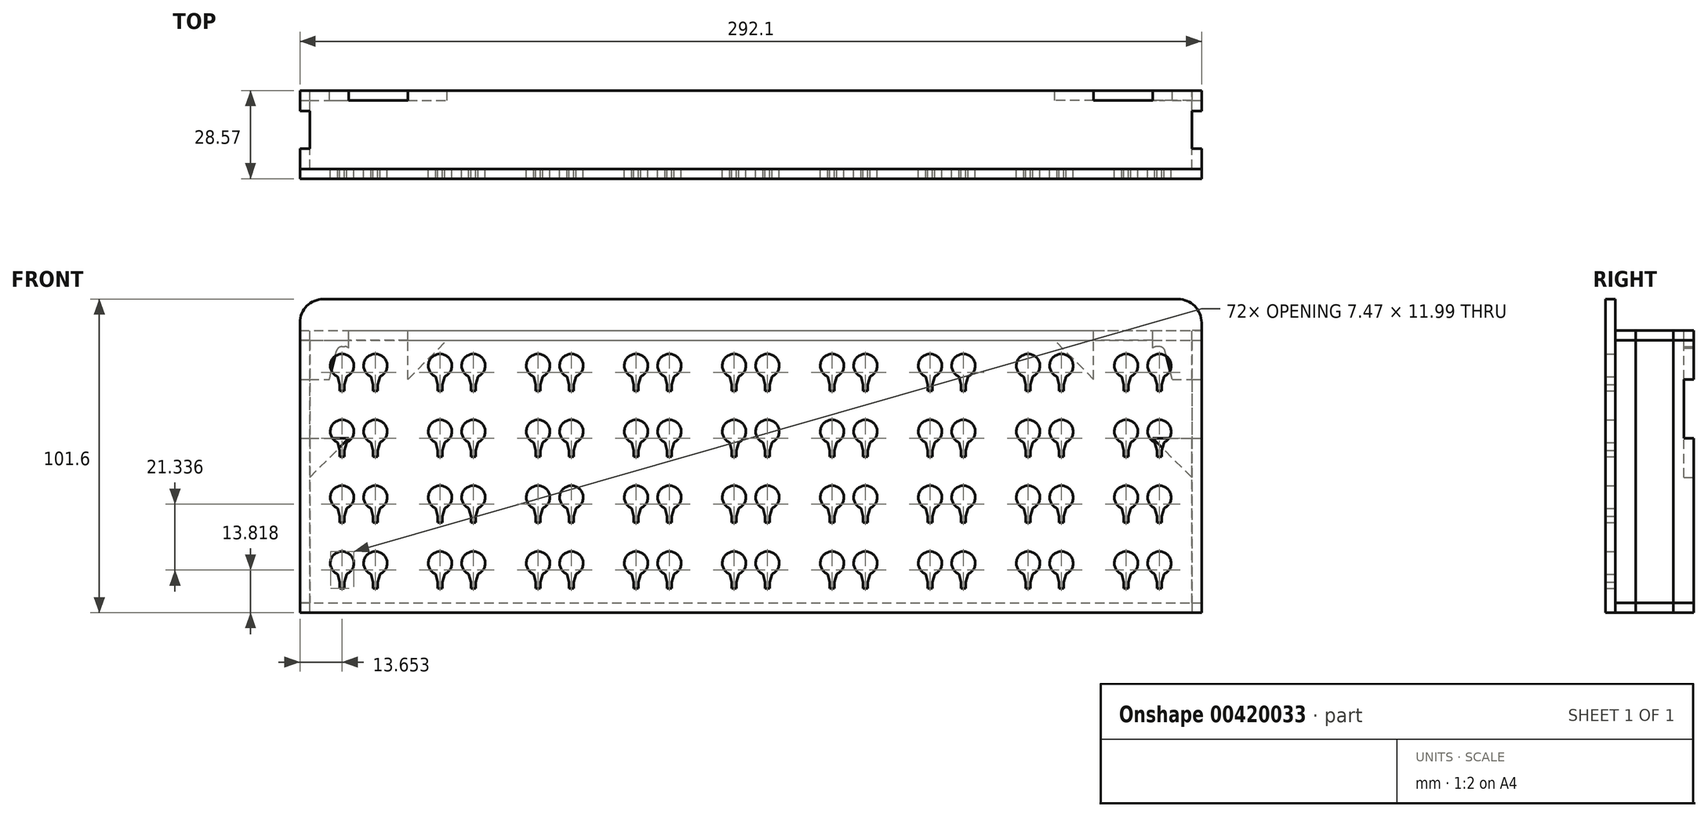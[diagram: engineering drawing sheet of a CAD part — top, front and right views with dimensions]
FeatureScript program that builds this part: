
annotation { "Feature Type Name" : "Feature", "Feature Type Description" : "" }
export const myFeature = defineFeature(function(context is Context, id is Id, definition is map)
    precondition{}
    {
        {
            var Q0;
            Q0=qCreatedBy(makeId("Front.planeOp"),FACE);
            var sketch = newSketch(context, id + "F0", { "sketchPlane" : qUnion([Q0])});
            skLineSegment(sketch, "E0.bottom", {"start": v(146.05, 50.8) * mm, "end": v(-146.05, 50.8) * mm});
            skLineSegment(sketch, "E0.top", {"start": v(146.05, -50.8) * mm, "end": v(-146.05, -50.8) * mm});
            skLineSegment(sketch, "E0.left", {"start": v(146.05, 50.8) * mm, "end": v(146.05, -50.8) * mm});
            skLineSegment(sketch, "E0.right", {"start": v(-146.05, 50.8) * mm, "end": v(-146.05, -50.8) * mm});
            skPoint(sketch, "E0.middle", {"position": v(0, 0) * mm});
            skLineSegment(sketch, "E1", {"start": v(-146.05, 29.21) * mm, "end": v(146.05, 29.21) * mm, "construction": true});
            skArc(sketch, "E2", {"start": v(-4.64, 25.48) * mm, "mid": v(-5.4, 33.02) * mm, "end": v(-6.16, 25.48) * mm});
            skLineSegment(sketch, "E3.bottom", {"start": v(-4.64, 21.03) * mm, "end": v(-6.16, 21.03) * mm});
            skLineSegment(sketch, "E3.left", {"start": v(-4.64, 21.03) * mm, "end": v(-4.64, 25.48) * mm});
            skLineSegment(sketch, "E3.right", {"start": v(-6.16, 21.03) * mm, "end": v(-6.16, 25.48) * mm});
            skPoint(sketch, "E3.middle", {"position": v(-5.4, 25.4) * mm});
            skLineSegment(sketch, "E4", {"start": v(0, 50.8) * mm, "end": v(0, -50.8) * mm, "construction": true});
            skLineSegment(sketch, "E5.MirrorCS", {"start": v(4.64, 21.03) * mm, "end": v(6.16, 21.03) * mm});
            skLineSegment(sketch, "E6.MirrorCS", {"start": v(4.64, 21.03) * mm, "end": v(4.64, 25.48) * mm});
            skLineSegment(sketch, "E7.MirrorCS", {"start": v(6.16, 21.03) * mm, "end": v(6.16, 25.48) * mm});
            skArc(sketch, "E8.MirrorCS", {"start": v(4.64, 25.48) * mm, "mid": v(5.4, 33.02) * mm, "end": v(6.16, 25.48) * mm});
            skArc(sketch, "E9.0.1.0", {"start": v(-4.64, 4.14) * mm, "mid": v(-5.4, 11.68) * mm, "end": v(-6.16, 4.14) * mm});
            skLineSegment(sketch, "E9.0.1.1", {"start": v(-4.64, -0.3) * mm, "end": v(-4.64, 4.14) * mm});
            skLineSegment(sketch, "E9.0.1.2", {"start": v(-4.64, -0.3) * mm, "end": v(-6.16, -0.3) * mm});
            skLineSegment(sketch, "E9.0.1.3", {"start": v(-6.16, -0.3) * mm, "end": v(-6.16, 4.14) * mm});
            skArc(sketch, "E9.0.1.4", {"start": v(4.64, 4.14) * mm, "mid": v(5.4, 11.68) * mm, "end": v(6.16, 4.14) * mm});
            skLineSegment(sketch, "E9.0.1.5", {"start": v(4.64, -0.3) * mm, "end": v(4.64, 4.14) * mm});
            skLineSegment(sketch, "E9.0.1.6", {"start": v(4.64, -0.3) * mm, "end": v(6.16, -0.3) * mm});
            skLineSegment(sketch, "E9.0.1.7", {"start": v(6.16, -0.3) * mm, "end": v(6.16, 4.14) * mm});
            skArc(sketch, "E9.0.2.0", {"start": v(-4.64, -17.2) * mm, "mid": v(-5.4, -9.65) * mm, "end": v(-6.16, -17.2) * mm});
            skLineSegment(sketch, "E9.0.2.1", {"start": v(-4.64, -21.64) * mm, "end": v(-4.64, -17.2) * mm});
            skLineSegment(sketch, "E9.0.2.2", {"start": v(-4.64, -21.64) * mm, "end": v(-6.16, -21.64) * mm});
            skLineSegment(sketch, "E9.0.2.3", {"start": v(-6.16, -21.64) * mm, "end": v(-6.16, -17.2) * mm});
            skArc(sketch, "E9.0.2.4", {"start": v(4.64, -17.2) * mm, "mid": v(5.4, -9.65) * mm, "end": v(6.16, -17.2) * mm});
            skLineSegment(sketch, "E9.0.2.5", {"start": v(4.64, -21.64) * mm, "end": v(4.64, -17.2) * mm});
            skLineSegment(sketch, "E9.0.2.6", {"start": v(4.64, -21.64) * mm, "end": v(6.16, -21.64) * mm});
            skLineSegment(sketch, "E9.0.2.7", {"start": v(6.16, -21.64) * mm, "end": v(6.16, -17.2) * mm});
            skArc(sketch, "E9.0.3.0", {"start": v(-4.64, -38.53) * mm, "mid": v(-5.4, -30.99) * mm, "end": v(-6.16, -38.53) * mm});
            skLineSegment(sketch, "E9.0.3.1", {"start": v(-4.64, -42.98) * mm, "end": v(-4.64, -38.53) * mm});
            skLineSegment(sketch, "E9.0.3.2", {"start": v(-4.64, -42.98) * mm, "end": v(-6.16, -42.98) * mm});
            skLineSegment(sketch, "E9.0.3.3", {"start": v(-6.16, -42.98) * mm, "end": v(-6.16, -38.53) * mm});
            skArc(sketch, "E9.0.3.4", {"start": v(4.64, -38.53) * mm, "mid": v(5.4, -30.99) * mm, "end": v(6.16, -38.53) * mm});
            skLineSegment(sketch, "E9.0.3.5", {"start": v(4.64, -42.98) * mm, "end": v(4.64, -38.53) * mm});
            skLineSegment(sketch, "E9.0.3.6", {"start": v(4.64, -42.98) * mm, "end": v(6.16, -42.98) * mm});
            skLineSegment(sketch, "E9.0.3.7", {"start": v(6.16, -42.98) * mm, "end": v(6.16, -38.53) * mm});
            skArc(sketch, "E9.1.0.0", {"start": v(27.11, 25.48) * mm, "mid": v(26.35, 33.02) * mm, "end": v(25.6, 25.48) * mm});
            skLineSegment(sketch, "E9.1.0.1", {"start": v(27.11, 21.03) * mm, "end": v(27.11, 25.48) * mm});
            skLineSegment(sketch, "E9.1.0.2", {"start": v(27.11, 21.03) * mm, "end": v(25.6, 21.03) * mm});
            skLineSegment(sketch, "E9.1.0.3", {"start": v(25.6, 21.03) * mm, "end": v(25.6, 25.48) * mm});
            skArc(sketch, "E9.1.0.4", {"start": v(36.39, 25.48) * mm, "mid": v(37.15, 33.02) * mm, "end": v(37.9, 25.48) * mm});
            skLineSegment(sketch, "E9.1.0.5", {"start": v(36.39, 21.03) * mm, "end": v(36.39, 25.48) * mm});
            skLineSegment(sketch, "E9.1.0.6", {"start": v(36.39, 21.03) * mm, "end": v(37.9, 21.03) * mm});
            skLineSegment(sketch, "E9.1.0.7", {"start": v(37.9, 21.03) * mm, "end": v(37.9, 25.48) * mm});
            skArc(sketch, "E9.1.1.0", {"start": v(27.11, 4.14) * mm, "mid": v(26.35, 11.68) * mm, "end": v(25.6, 4.14) * mm});
            skLineSegment(sketch, "E9.1.1.1", {"start": v(27.11, -0.3) * mm, "end": v(27.11, 4.14) * mm});
            skLineSegment(sketch, "E9.1.1.2", {"start": v(27.11, -0.3) * mm, "end": v(25.6, -0.3) * mm});
            skLineSegment(sketch, "E9.1.1.3", {"start": v(25.6, -0.3) * mm, "end": v(25.6, 4.14) * mm});
            skArc(sketch, "E9.1.1.4", {"start": v(36.39, 4.14) * mm, "mid": v(37.15, 11.68) * mm, "end": v(37.9, 4.14) * mm});
            skLineSegment(sketch, "E9.1.1.5", {"start": v(36.39, -0.3) * mm, "end": v(36.39, 4.14) * mm});
            skLineSegment(sketch, "E9.1.1.6", {"start": v(36.39, -0.3) * mm, "end": v(37.9, -0.3) * mm});
            skLineSegment(sketch, "E9.1.1.7", {"start": v(37.9, -0.3) * mm, "end": v(37.9, 4.14) * mm});
            skArc(sketch, "E9.1.2.0", {"start": v(27.11, -17.2) * mm, "mid": v(26.35, -9.65) * mm, "end": v(25.6, -17.2) * mm});
            skLineSegment(sketch, "E9.1.2.1", {"start": v(27.11, -21.64) * mm, "end": v(27.11, -17.2) * mm});
            skLineSegment(sketch, "E9.1.2.2", {"start": v(27.11, -21.64) * mm, "end": v(25.6, -21.64) * mm});
            skLineSegment(sketch, "E9.1.2.3", {"start": v(25.6, -21.64) * mm, "end": v(25.6, -17.2) * mm});
            skArc(sketch, "E9.1.2.4", {"start": v(36.39, -17.2) * mm, "mid": v(37.15, -9.65) * mm, "end": v(37.9, -17.2) * mm});
            skLineSegment(sketch, "E9.1.2.5", {"start": v(36.39, -21.64) * mm, "end": v(36.39, -17.2) * mm});
            skLineSegment(sketch, "E9.1.2.6", {"start": v(36.39, -21.64) * mm, "end": v(37.9, -21.64) * mm});
            skLineSegment(sketch, "E9.1.2.7", {"start": v(37.9, -21.64) * mm, "end": v(37.9, -17.2) * mm});
            skArc(sketch, "E9.1.3.0", {"start": v(27.11, -38.53) * mm, "mid": v(26.35, -30.99) * mm, "end": v(25.6, -38.53) * mm});
            skLineSegment(sketch, "E9.1.3.1", {"start": v(27.11, -42.98) * mm, "end": v(27.11, -38.53) * mm});
            skLineSegment(sketch, "E9.1.3.2", {"start": v(27.11, -42.98) * mm, "end": v(25.6, -42.98) * mm});
            skLineSegment(sketch, "E9.1.3.3", {"start": v(25.6, -42.98) * mm, "end": v(25.6, -38.53) * mm});
            skArc(sketch, "E9.1.3.4", {"start": v(36.39, -38.53) * mm, "mid": v(37.15, -30.99) * mm, "end": v(37.9, -38.53) * mm});
            skLineSegment(sketch, "E9.1.3.5", {"start": v(36.39, -42.98) * mm, "end": v(36.39, -38.53) * mm});
            skLineSegment(sketch, "E9.1.3.6", {"start": v(36.39, -42.98) * mm, "end": v(37.9, -42.98) * mm});
            skLineSegment(sketch, "E9.1.3.7", {"start": v(37.9, -42.98) * mm, "end": v(37.9, -38.53) * mm});
            skArc(sketch, "E9.2.0.0", {"start": v(58.86, 25.48) * mm, "mid": v(58.1, 33.02) * mm, "end": v(57.34, 25.48) * mm});
            skLineSegment(sketch, "E9.2.0.1", {"start": v(58.86, 21.03) * mm, "end": v(58.86, 25.48) * mm});
            skLineSegment(sketch, "E9.2.0.2", {"start": v(58.86, 21.03) * mm, "end": v(57.34, 21.03) * mm});
            skLineSegment(sketch, "E9.2.0.3", {"start": v(57.34, 21.03) * mm, "end": v(57.34, 25.48) * mm});
            skArc(sketch, "E9.2.0.4", {"start": v(68.14, 25.48) * mm, "mid": v(68.9, 33.02) * mm, "end": v(69.66, 25.48) * mm});
            skLineSegment(sketch, "E9.2.0.5", {"start": v(68.14, 21.03) * mm, "end": v(68.14, 25.48) * mm});
            skLineSegment(sketch, "E9.2.0.6", {"start": v(68.14, 21.03) * mm, "end": v(69.66, 21.03) * mm});
            skLineSegment(sketch, "E9.2.0.7", {"start": v(69.66, 21.03) * mm, "end": v(69.66, 25.48) * mm});
            skArc(sketch, "E9.2.1.0", {"start": v(58.86, 4.14) * mm, "mid": v(58.1, 11.68) * mm, "end": v(57.34, 4.14) * mm});
            skLineSegment(sketch, "E9.2.1.1", {"start": v(58.86, -0.3) * mm, "end": v(58.86, 4.14) * mm});
            skLineSegment(sketch, "E9.2.1.2", {"start": v(58.86, -0.3) * mm, "end": v(57.34, -0.3) * mm});
            skLineSegment(sketch, "E9.2.1.3", {"start": v(57.34, -0.3) * mm, "end": v(57.34, 4.14) * mm});
            skArc(sketch, "E9.2.1.4", {"start": v(68.14, 4.14) * mm, "mid": v(68.9, 11.68) * mm, "end": v(69.66, 4.14) * mm});
            skLineSegment(sketch, "E9.2.1.5", {"start": v(68.14, -0.3) * mm, "end": v(68.14, 4.14) * mm});
            skLineSegment(sketch, "E9.2.1.6", {"start": v(68.14, -0.3) * mm, "end": v(69.66, -0.3) * mm});
            skLineSegment(sketch, "E9.2.1.7", {"start": v(69.66, -0.3) * mm, "end": v(69.66, 4.14) * mm});
            skArc(sketch, "E9.2.2.0", {"start": v(58.86, -17.2) * mm, "mid": v(58.1, -9.65) * mm, "end": v(57.34, -17.2) * mm});
            skLineSegment(sketch, "E9.2.2.1", {"start": v(58.86, -21.64) * mm, "end": v(58.86, -17.2) * mm});
            skLineSegment(sketch, "E9.2.2.2", {"start": v(58.86, -21.64) * mm, "end": v(57.34, -21.64) * mm});
            skLineSegment(sketch, "E9.2.2.3", {"start": v(57.34, -21.64) * mm, "end": v(57.34, -17.2) * mm});
            skArc(sketch, "E9.2.2.4", {"start": v(68.14, -17.2) * mm, "mid": v(68.9, -9.65) * mm, "end": v(69.66, -17.2) * mm});
            skLineSegment(sketch, "E9.2.2.5", {"start": v(68.14, -21.64) * mm, "end": v(68.14, -17.2) * mm});
            skLineSegment(sketch, "E9.2.2.6", {"start": v(68.14, -21.64) * mm, "end": v(69.66, -21.64) * mm});
            skLineSegment(sketch, "E9.2.2.7", {"start": v(69.66, -21.64) * mm, "end": v(69.66, -17.2) * mm});
            skArc(sketch, "E9.2.3.0", {"start": v(58.86, -38.53) * mm, "mid": v(58.1, -30.99) * mm, "end": v(57.34, -38.53) * mm});
            skLineSegment(sketch, "E9.2.3.1", {"start": v(58.86, -42.98) * mm, "end": v(58.86, -38.53) * mm});
            skLineSegment(sketch, "E9.2.3.2", {"start": v(58.86, -42.98) * mm, "end": v(57.34, -42.98) * mm});
            skLineSegment(sketch, "E9.2.3.3", {"start": v(57.34, -42.98) * mm, "end": v(57.34, -38.53) * mm});
            skArc(sketch, "E9.2.3.4", {"start": v(68.14, -38.53) * mm, "mid": v(68.9, -30.99) * mm, "end": v(69.66, -38.53) * mm});
            skLineSegment(sketch, "E9.2.3.5", {"start": v(68.14, -42.98) * mm, "end": v(68.14, -38.53) * mm});
            skLineSegment(sketch, "E9.2.3.6", {"start": v(68.14, -42.98) * mm, "end": v(69.66, -42.98) * mm});
            skLineSegment(sketch, "E9.2.3.7", {"start": v(69.66, -42.98) * mm, "end": v(69.66, -38.53) * mm});
            skArc(sketch, "E9.3.0.0", {"start": v(90.61, 25.48) * mm, "mid": v(89.85, 33.02) * mm, "end": v(89.1, 25.48) * mm});
            skLineSegment(sketch, "E9.3.0.1", {"start": v(90.61, 21.03) * mm, "end": v(90.61, 25.48) * mm});
            skLineSegment(sketch, "E9.3.0.2", {"start": v(90.61, 21.03) * mm, "end": v(89.1, 21.03) * mm});
            skLineSegment(sketch, "E9.3.0.3", {"start": v(89.1, 21.03) * mm, "end": v(89.1, 25.48) * mm});
            skArc(sketch, "E9.3.0.4", {"start": v(99.89, 25.48) * mm, "mid": v(100.65, 33.02) * mm, "end": v(101.4, 25.48) * mm});
            skLineSegment(sketch, "E9.3.0.5", {"start": v(99.89, 21.03) * mm, "end": v(99.89, 25.48) * mm});
            skLineSegment(sketch, "E9.3.0.6", {"start": v(99.89, 21.03) * mm, "end": v(101.4, 21.03) * mm});
            skLineSegment(sketch, "E9.3.0.7", {"start": v(101.4, 21.03) * mm, "end": v(101.4, 25.48) * mm});
            skArc(sketch, "E9.3.1.0", {"start": v(90.61, 4.14) * mm, "mid": v(89.85, 11.68) * mm, "end": v(89.1, 4.14) * mm});
            skLineSegment(sketch, "E9.3.1.1", {"start": v(90.61, -0.3) * mm, "end": v(90.61, 4.14) * mm});
            skLineSegment(sketch, "E9.3.1.2", {"start": v(90.61, -0.3) * mm, "end": v(89.1, -0.3) * mm});
            skLineSegment(sketch, "E9.3.1.3", {"start": v(89.1, -0.3) * mm, "end": v(89.1, 4.14) * mm});
            skArc(sketch, "E9.3.1.4", {"start": v(99.89, 4.14) * mm, "mid": v(100.65, 11.68) * mm, "end": v(101.4, 4.14) * mm});
            skLineSegment(sketch, "E9.3.1.5", {"start": v(99.89, -0.3) * mm, "end": v(99.89, 4.14) * mm});
            skLineSegment(sketch, "E9.3.1.6", {"start": v(99.89, -0.3) * mm, "end": v(101.4, -0.3) * mm});
            skLineSegment(sketch, "E9.3.1.7", {"start": v(101.4, -0.3) * mm, "end": v(101.4, 4.14) * mm});
            skArc(sketch, "E9.3.2.0", {"start": v(90.61, -17.2) * mm, "mid": v(89.85, -9.65) * mm, "end": v(89.1, -17.2) * mm});
            skLineSegment(sketch, "E9.3.2.1", {"start": v(90.61, -21.64) * mm, "end": v(90.61, -17.2) * mm});
            skLineSegment(sketch, "E9.3.2.2", {"start": v(90.61, -21.64) * mm, "end": v(89.1, -21.64) * mm});
            skLineSegment(sketch, "E9.3.2.3", {"start": v(89.1, -21.64) * mm, "end": v(89.1, -17.2) * mm});
            skArc(sketch, "E9.3.2.4", {"start": v(99.89, -17.2) * mm, "mid": v(100.65, -9.65) * mm, "end": v(101.4, -17.2) * mm});
            skLineSegment(sketch, "E9.3.2.5", {"start": v(99.89, -21.64) * mm, "end": v(99.89, -17.2) * mm});
            skLineSegment(sketch, "E9.3.2.6", {"start": v(99.89, -21.64) * mm, "end": v(101.4, -21.64) * mm});
            skLineSegment(sketch, "E9.3.2.7", {"start": v(101.4, -21.64) * mm, "end": v(101.4, -17.2) * mm});
            skArc(sketch, "E9.3.3.0", {"start": v(90.61, -38.53) * mm, "mid": v(89.85, -30.99) * mm, "end": v(89.1, -38.53) * mm});
            skLineSegment(sketch, "E9.3.3.1", {"start": v(90.61, -42.98) * mm, "end": v(90.61, -38.53) * mm});
            skLineSegment(sketch, "E9.3.3.2", {"start": v(90.61, -42.98) * mm, "end": v(89.1, -42.98) * mm});
            skLineSegment(sketch, "E9.3.3.3", {"start": v(89.1, -42.98) * mm, "end": v(89.1, -38.53) * mm});
            skArc(sketch, "E9.3.3.4", {"start": v(99.89, -38.53) * mm, "mid": v(100.65, -30.99) * mm, "end": v(101.4, -38.53) * mm});
            skLineSegment(sketch, "E9.3.3.5", {"start": v(99.89, -42.98) * mm, "end": v(99.89, -38.53) * mm});
            skLineSegment(sketch, "E9.3.3.6", {"start": v(99.89, -42.98) * mm, "end": v(101.4, -42.98) * mm});
            skLineSegment(sketch, "E9.3.3.7", {"start": v(101.4, -42.98) * mm, "end": v(101.4, -38.53) * mm});
            skArc(sketch, "E9.4.0.0", {"start": v(122.36, 25.48) * mm, "mid": v(121.6, 33.02) * mm, "end": v(120.84, 25.48) * mm});
            skLineSegment(sketch, "E9.4.0.1", {"start": v(122.36, 21.03) * mm, "end": v(122.36, 25.48) * mm});
            skLineSegment(sketch, "E9.4.0.2", {"start": v(122.36, 21.03) * mm, "end": v(120.84, 21.03) * mm});
            skLineSegment(sketch, "E9.4.0.3", {"start": v(120.84, 21.03) * mm, "end": v(120.84, 25.48) * mm});
            skArc(sketch, "E9.4.0.4", {"start": v(131.64, 25.48) * mm, "mid": v(132.4, 33.02) * mm, "end": v(133.16, 25.48) * mm});
            skLineSegment(sketch, "E9.4.0.5", {"start": v(131.64, 21.03) * mm, "end": v(131.64, 25.48) * mm});
            skLineSegment(sketch, "E9.4.0.6", {"start": v(131.64, 21.03) * mm, "end": v(133.16, 21.03) * mm});
            skLineSegment(sketch, "E9.4.0.7", {"start": v(133.16, 21.03) * mm, "end": v(133.16, 25.48) * mm});
            skArc(sketch, "E9.4.1.0", {"start": v(122.36, 4.14) * mm, "mid": v(121.6, 11.68) * mm, "end": v(120.84, 4.14) * mm});
            skLineSegment(sketch, "E9.4.1.1", {"start": v(122.36, -0.3) * mm, "end": v(122.36, 4.14) * mm});
            skLineSegment(sketch, "E9.4.1.2", {"start": v(122.36, -0.3) * mm, "end": v(120.84, -0.3) * mm});
            skLineSegment(sketch, "E9.4.1.3", {"start": v(120.84, -0.3) * mm, "end": v(120.84, 4.14) * mm});
            skArc(sketch, "E9.4.1.4", {"start": v(131.64, 4.14) * mm, "mid": v(132.4, 11.68) * mm, "end": v(133.16, 4.14) * mm});
            skLineSegment(sketch, "E9.4.1.5", {"start": v(131.64, -0.3) * mm, "end": v(131.64, 4.14) * mm});
            skLineSegment(sketch, "E9.4.1.6", {"start": v(131.64, -0.3) * mm, "end": v(133.16, -0.3) * mm});
            skLineSegment(sketch, "E9.4.1.7", {"start": v(133.16, -0.3) * mm, "end": v(133.16, 4.14) * mm});
            skArc(sketch, "E9.4.2.0", {"start": v(122.36, -17.2) * mm, "mid": v(121.6, -9.65) * mm, "end": v(120.84, -17.2) * mm});
            skLineSegment(sketch, "E9.4.2.1", {"start": v(122.36, -21.64) * mm, "end": v(122.36, -17.2) * mm});
            skLineSegment(sketch, "E9.4.2.2", {"start": v(122.36, -21.64) * mm, "end": v(120.84, -21.64) * mm});
            skLineSegment(sketch, "E9.4.2.3", {"start": v(120.84, -21.64) * mm, "end": v(120.84, -17.2) * mm});
            skArc(sketch, "E9.4.2.4", {"start": v(131.64, -17.2) * mm, "mid": v(132.4, -9.65) * mm, "end": v(133.16, -17.2) * mm});
            skLineSegment(sketch, "E9.4.2.5", {"start": v(131.64, -21.64) * mm, "end": v(131.64, -17.2) * mm});
            skLineSegment(sketch, "E9.4.2.6", {"start": v(131.64, -21.64) * mm, "end": v(133.16, -21.64) * mm});
            skLineSegment(sketch, "E9.4.2.7", {"start": v(133.16, -21.64) * mm, "end": v(133.16, -17.2) * mm});
            skArc(sketch, "E9.4.3.0", {"start": v(122.36, -38.53) * mm, "mid": v(121.6, -30.99) * mm, "end": v(120.84, -38.53) * mm});
            skLineSegment(sketch, "E9.4.3.1", {"start": v(122.36, -42.98) * mm, "end": v(122.36, -38.53) * mm});
            skLineSegment(sketch, "E9.4.3.2", {"start": v(122.36, -42.98) * mm, "end": v(120.84, -42.98) * mm});
            skLineSegment(sketch, "E9.4.3.3", {"start": v(120.84, -42.98) * mm, "end": v(120.84, -38.53) * mm});
            skArc(sketch, "E9.4.3.4", {"start": v(131.64, -38.53) * mm, "mid": v(132.4, -30.99) * mm, "end": v(133.16, -38.53) * mm});
            skLineSegment(sketch, "E9.4.3.5", {"start": v(131.64, -42.98) * mm, "end": v(131.64, -38.53) * mm});
            skLineSegment(sketch, "E9.4.3.6", {"start": v(131.64, -42.98) * mm, "end": v(133.16, -42.98) * mm});
            skLineSegment(sketch, "E9.4.3.7", {"start": v(133.16, -42.98) * mm, "end": v(133.16, -38.53) * mm});
            skLineSegment(sketch, "E9.direction1", {"start": v(-6.16, 21.03) * mm, "end": v(25.6, 21.03) * mm, "construction": true});
            skLineSegment(sketch, "E9.direction2", {"start": v(-6.16, 21.03) * mm, "end": v(-6.16, -0.3) * mm, "construction": true});
            skLineSegment(sketch, "E10.MirrorCS", {"start": v(-27.11, 21.03) * mm, "end": v(-25.6, 21.03) * mm});
            skLineSegment(sketch, "E11.MirrorCS", {"start": v(-57.34, -42.98) * mm, "end": v(-57.34, -38.53) * mm});
            skLineSegment(sketch, "E12.MirrorCS", {"start": v(-89.1, -0.3) * mm, "end": v(-89.1, 4.14) * mm});
            skLineSegment(sketch, "E13.MirrorCS", {"start": v(-89.1, -42.98) * mm, "end": v(-89.1, -38.53) * mm});
            skLineSegment(sketch, "E14.MirrorCS", {"start": v(-120.84, -0.3) * mm, "end": v(-120.84, 4.14) * mm});
            skLineSegment(sketch, "E15.MirrorCS", {"start": v(-25.6, -0.3) * mm, "end": v(-25.6, 4.14) * mm});
            skLineSegment(sketch, "E16.MirrorCS", {"start": v(-25.6, -42.98) * mm, "end": v(-25.6, -38.53) * mm});
            skLineSegment(sketch, "E17.MirrorCS", {"start": v(-57.34, -0.3) * mm, "end": v(-57.34, 4.14) * mm});
            skLineSegment(sketch, "E18.MirrorCS", {"start": v(-120.84, -42.98) * mm, "end": v(-120.84, -38.53) * mm});
            skLineSegment(sketch, "E19.MirrorCS", {"start": v(-27.11, -0.3) * mm, "end": v(-25.6, -0.3) * mm});
            skLineSegment(sketch, "E20.MirrorCS", {"start": v(-27.11, -42.98) * mm, "end": v(-25.6, -42.98) * mm});
            skLineSegment(sketch, "E21.MirrorCS", {"start": v(-58.86, -0.3) * mm, "end": v(-57.34, -0.3) * mm});
            skLineSegment(sketch, "E22.MirrorCS", {"start": v(-122.36, -42.98) * mm, "end": v(-120.84, -42.98) * mm});
            skLineSegment(sketch, "E23.MirrorCS", {"start": v(-58.86, -42.98) * mm, "end": v(-57.34, -42.98) * mm});
            skLineSegment(sketch, "E24.MirrorCS", {"start": v(-90.61, -0.3) * mm, "end": v(-89.1, -0.3) * mm});
            skLineSegment(sketch, "E25.MirrorCS", {"start": v(-90.61, -42.98) * mm, "end": v(-89.1, -42.98) * mm});
            skLineSegment(sketch, "E26.MirrorCS", {"start": v(-122.36, -0.3) * mm, "end": v(-120.84, -0.3) * mm});
            skLineSegment(sketch, "E27.MirrorCS", {"start": v(-122.36, -42.98) * mm, "end": v(-122.36, -38.53) * mm});
            skLineSegment(sketch, "E28.MirrorCS", {"start": v(-58.86, -42.98) * mm, "end": v(-58.86, -38.53) * mm});
            skLineSegment(sketch, "E29.MirrorCS", {"start": v(-90.61, -0.3) * mm, "end": v(-90.61, 4.14) * mm});
            skLineSegment(sketch, "E30.MirrorCS", {"start": v(-90.61, -42.98) * mm, "end": v(-90.61, -38.53) * mm});
            skLineSegment(sketch, "E31.MirrorCS", {"start": v(-122.36, -0.3) * mm, "end": v(-122.36, 4.14) * mm});
            skLineSegment(sketch, "E32.MirrorCS", {"start": v(-27.11, -0.3) * mm, "end": v(-27.11, 4.14) * mm});
            skLineSegment(sketch, "E33.MirrorCS", {"start": v(-27.11, -42.98) * mm, "end": v(-27.11, -38.53) * mm});
            skLineSegment(sketch, "E34.MirrorCS", {"start": v(-58.86, -0.3) * mm, "end": v(-58.86, 4.14) * mm});
            skLineSegment(sketch, "E35.MirrorCS", {"start": v(-131.64, 21.03) * mm, "end": v(-133.16, 21.03) * mm});
            skLineSegment(sketch, "E36.MirrorCS", {"start": v(-131.64, -21.64) * mm, "end": v(-133.16, -21.64) * mm});
            skLineSegment(sketch, "E37.MirrorCS", {"start": v(-68.14, 21.03) * mm, "end": v(-69.66, 21.03) * mm});
            skLineSegment(sketch, "E38.MirrorCS", {"start": v(-68.14, -21.64) * mm, "end": v(-69.66, -21.64) * mm});
            skLineSegment(sketch, "E39.MirrorCS", {"start": v(-99.89, 21.03) * mm, "end": v(-101.4, 21.03) * mm});
            skLineSegment(sketch, "E40.MirrorCS", {"start": v(-99.89, -21.64) * mm, "end": v(-101.4, -21.64) * mm});
            skLineSegment(sketch, "E41.MirrorCS", {"start": v(-36.39, 21.03) * mm, "end": v(-37.9, 21.03) * mm});
            skLineSegment(sketch, "E42.MirrorCS", {"start": v(-36.39, -21.64) * mm, "end": v(-37.9, -21.64) * mm});
            skLineSegment(sketch, "E43.MirrorCS", {"start": v(-133.16, -21.64) * mm, "end": v(-133.16, -17.2) * mm});
            skLineSegment(sketch, "E44.MirrorCS", {"start": v(-69.66, -21.64) * mm, "end": v(-69.66, -17.2) * mm});
            skLineSegment(sketch, "E45.MirrorCS", {"start": v(-101.4, 21.03) * mm, "end": v(-101.4, 25.48) * mm});
            skLineSegment(sketch, "E46.MirrorCS", {"start": v(-101.4, -21.64) * mm, "end": v(-101.4, -17.2) * mm});
            skLineSegment(sketch, "E47.MirrorCS", {"start": v(-133.16, 21.03) * mm, "end": v(-133.16, 25.48) * mm});
            skLineSegment(sketch, "E48.MirrorCS", {"start": v(-37.9, 21.03) * mm, "end": v(-37.9, 25.48) * mm});
            skLineSegment(sketch, "E49.MirrorCS", {"start": v(-37.9, -21.64) * mm, "end": v(-37.9, -17.2) * mm});
            skLineSegment(sketch, "E50.MirrorCS", {"start": v(-69.66, 21.03) * mm, "end": v(-69.66, 25.48) * mm});
            skLineSegment(sketch, "E51.MirrorCS", {"start": v(-131.64, 21.03) * mm, "end": v(-131.64, 25.48) * mm});
            skLineSegment(sketch, "E52.MirrorCS", {"start": v(-131.64, -21.64) * mm, "end": v(-131.64, -17.2) * mm});
            skLineSegment(sketch, "E53.MirrorCS", {"start": v(-68.14, 21.03) * mm, "end": v(-68.14, 25.48) * mm});
            skLineSegment(sketch, "E54.MirrorCS", {"start": v(-68.14, -21.64) * mm, "end": v(-68.14, -17.2) * mm});
            skLineSegment(sketch, "E55.MirrorCS", {"start": v(-99.89, 21.03) * mm, "end": v(-99.89, 25.48) * mm});
            skLineSegment(sketch, "E56.MirrorCS", {"start": v(-99.89, -21.64) * mm, "end": v(-99.89, -17.2) * mm});
            skLineSegment(sketch, "E57.MirrorCS", {"start": v(-36.39, 21.03) * mm, "end": v(-36.39, 25.48) * mm});
            skLineSegment(sketch, "E58.MirrorCS", {"start": v(-36.39, -21.64) * mm, "end": v(-36.39, -17.2) * mm});
            skLineSegment(sketch, "E59.MirrorCS", {"start": v(-120.84, 21.03) * mm, "end": v(-120.84, 25.48) * mm});
            skLineSegment(sketch, "E60.MirrorCS", {"start": v(-120.84, -21.64) * mm, "end": v(-120.84, -17.2) * mm});
            skLineSegment(sketch, "E61.MirrorCS", {"start": v(-57.34, 21.03) * mm, "end": v(-57.34, 25.48) * mm});
            skLineSegment(sketch, "E62.MirrorCS", {"start": v(-57.34, -21.64) * mm, "end": v(-57.34, -17.2) * mm});
            skLineSegment(sketch, "E63.MirrorCS", {"start": v(-89.1, 21.03) * mm, "end": v(-89.1, 25.48) * mm});
            skLineSegment(sketch, "E64.MirrorCS", {"start": v(-89.1, -21.64) * mm, "end": v(-89.1, -17.2) * mm});
            skLineSegment(sketch, "E65.MirrorCS", {"start": v(-25.6, 21.03) * mm, "end": v(-25.6, 25.48) * mm});
            skLineSegment(sketch, "E66.MirrorCS", {"start": v(-25.6, -21.64) * mm, "end": v(-25.6, -17.2) * mm});
            skLineSegment(sketch, "E67.MirrorCS", {"start": v(-122.36, 21.03) * mm, "end": v(-120.84, 21.03) * mm});
            skLineSegment(sketch, "E68.MirrorCS", {"start": v(-122.36, -21.64) * mm, "end": v(-120.84, -21.64) * mm});
            skLineSegment(sketch, "E69.MirrorCS", {"start": v(-58.86, 21.03) * mm, "end": v(-57.34, 21.03) * mm});
            skLineSegment(sketch, "E70.MirrorCS", {"start": v(-58.86, -21.64) * mm, "end": v(-57.34, -21.64) * mm});
            skLineSegment(sketch, "E71.MirrorCS", {"start": v(-90.61, 21.03) * mm, "end": v(-89.1, 21.03) * mm});
            skLineSegment(sketch, "E72.MirrorCS", {"start": v(-90.61, -21.64) * mm, "end": v(-89.1, -21.64) * mm});
            skLineSegment(sketch, "E73.MirrorCS", {"start": v(-27.11, -21.64) * mm, "end": v(-25.6, -21.64) * mm});
            skLineSegment(sketch, "E74.MirrorCS", {"start": v(-122.36, 21.03) * mm, "end": v(-122.36, 25.48) * mm});
            skLineSegment(sketch, "E75.MirrorCS", {"start": v(-122.36, -21.64) * mm, "end": v(-122.36, -17.2) * mm});
            skLineSegment(sketch, "E76.MirrorCS", {"start": v(-58.86, 21.03) * mm, "end": v(-58.86, 25.48) * mm});
            skLineSegment(sketch, "E77.MirrorCS", {"start": v(-58.86, -21.64) * mm, "end": v(-58.86, -17.2) * mm});
            skLineSegment(sketch, "E78.MirrorCS", {"start": v(-90.61, 21.03) * mm, "end": v(-90.61, 25.48) * mm});
            skLineSegment(sketch, "E79.MirrorCS", {"start": v(-90.61, -21.64) * mm, "end": v(-90.61, -17.2) * mm});
            skLineSegment(sketch, "E80.MirrorCS", {"start": v(-27.11, 21.03) * mm, "end": v(-27.11, 25.48) * mm});
            skLineSegment(sketch, "E81.MirrorCS", {"start": v(-27.11, -21.64) * mm, "end": v(-27.11, -17.2) * mm});
            skLineSegment(sketch, "E82.MirrorCS", {"start": v(-68.14, -0.3) * mm, "end": v(-68.14, 4.14) * mm});
            skLineSegment(sketch, "E83.MirrorCS", {"start": v(-36.39, -42.98) * mm, "end": v(-36.39, -38.53) * mm});
            skLineSegment(sketch, "E84.MirrorCS", {"start": v(-36.39, -0.3) * mm, "end": v(-36.39, 4.14) * mm});
            skLineSegment(sketch, "E85.MirrorCS", {"start": v(-131.64, -0.3) * mm, "end": v(-131.64, 4.14) * mm});
            skLineSegment(sketch, "E86.MirrorCS", {"start": v(-99.89, -42.98) * mm, "end": v(-99.89, -38.53) * mm});
            skLineSegment(sketch, "E87.MirrorCS", {"start": v(-99.89, -0.3) * mm, "end": v(-99.89, 4.14) * mm});
            skLineSegment(sketch, "E88.MirrorCS", {"start": v(-68.14, -42.98) * mm, "end": v(-68.14, -38.53) * mm});
            skLineSegment(sketch, "E89.MirrorCS", {"start": v(-131.64, -42.98) * mm, "end": v(-131.64, -38.53) * mm});
            skLineSegment(sketch, "E90.MirrorCS", {"start": v(-69.66, -42.98) * mm, "end": v(-69.66, -38.53) * mm});
            skLineSegment(sketch, "E91.MirrorCS", {"start": v(-131.64, -42.98) * mm, "end": v(-133.16, -42.98) * mm});
            skLineSegment(sketch, "E92.MirrorCS", {"start": v(-99.89, -42.98) * mm, "end": v(-101.4, -42.98) * mm});
            skLineSegment(sketch, "E93.MirrorCS", {"start": v(-131.64, -0.3) * mm, "end": v(-133.16, -0.3) * mm});
            skLineSegment(sketch, "E94.MirrorCS", {"start": v(-68.14, -0.3) * mm, "end": v(-69.66, -0.3) * mm});
            skLineSegment(sketch, "E95.MirrorCS", {"start": v(-101.4, -0.3) * mm, "end": v(-101.4, 4.14) * mm});
            skLineSegment(sketch, "E96.MirrorCS", {"start": v(-37.9, -42.98) * mm, "end": v(-37.9, -38.53) * mm});
            skLineSegment(sketch, "E97.MirrorCS", {"start": v(-133.16, -0.3) * mm, "end": v(-133.16, 4.14) * mm});
            skLineSegment(sketch, "E98.MirrorCS", {"start": v(-99.89, -0.3) * mm, "end": v(-101.4, -0.3) * mm});
            skLineSegment(sketch, "E99.MirrorCS", {"start": v(-37.9, -0.3) * mm, "end": v(-37.9, 4.14) * mm});
            skLineSegment(sketch, "E100.MirrorCS", {"start": v(-36.39, -0.3) * mm, "end": v(-37.9, -0.3) * mm});
            skLineSegment(sketch, "E101.MirrorCS", {"start": v(-69.66, -0.3) * mm, "end": v(-69.66, 4.14) * mm});
            skLineSegment(sketch, "E102.MirrorCS", {"start": v(-101.4, -42.98) * mm, "end": v(-101.4, -38.53) * mm});
            skLineSegment(sketch, "E103.MirrorCS", {"start": v(-133.16, -42.98) * mm, "end": v(-133.16, -38.53) * mm});
            skLineSegment(sketch, "E104.MirrorCS", {"start": v(-68.14, -42.98) * mm, "end": v(-69.66, -42.98) * mm});
            skLineSegment(sketch, "E105.MirrorCS", {"start": v(-36.39, -42.98) * mm, "end": v(-37.9, -42.98) * mm});
            skArc(sketch, "E106.MirrorCS", {"start": v(-131.64, -38.53) * mm, "mid": v(-132.4, -30.99) * mm, "end": v(-133.16, -38.53) * mm});
            skArc(sketch, "E107.MirrorCS", {"start": v(-68.14, -38.53) * mm, "mid": v(-68.9, -30.99) * mm, "end": v(-69.66, -38.53) * mm});
            skArc(sketch, "E108.MirrorCS", {"start": v(-99.89, 4.14) * mm, "mid": v(-100.65, 11.68) * mm, "end": v(-101.4, 4.14) * mm});
            skArc(sketch, "E109.MirrorCS", {"start": v(-99.89, -38.53) * mm, "mid": v(-100.65, -30.99) * mm, "end": v(-101.4, -38.53) * mm});
            skArc(sketch, "E110.MirrorCS", {"start": v(-131.64, 4.14) * mm, "mid": v(-132.4, 11.68) * mm, "end": v(-133.16, 4.14) * mm});
            skArc(sketch, "E111.MirrorCS", {"start": v(-36.39, 4.14) * mm, "mid": v(-37.15, 11.68) * mm, "end": v(-37.9, 4.14) * mm});
            skArc(sketch, "E112.MirrorCS", {"start": v(-36.39, -38.53) * mm, "mid": v(-37.15, -30.99) * mm, "end": v(-37.9, -38.53) * mm});
            skArc(sketch, "E113.MirrorCS", {"start": v(-68.14, 4.14) * mm, "mid": v(-68.9, 11.68) * mm, "end": v(-69.66, 4.14) * mm});
            skArc(sketch, "E114.MirrorCS", {"start": v(-122.36, -38.53) * mm, "mid": v(-121.6, -30.99) * mm, "end": v(-120.84, -38.53) * mm});
            skArc(sketch, "E115.MirrorCS", {"start": v(-58.86, -38.53) * mm, "mid": v(-58.1, -30.99) * mm, "end": v(-57.34, -38.53) * mm});
            skArc(sketch, "E116.MirrorCS", {"start": v(-90.61, 4.14) * mm, "mid": v(-89.85, 11.68) * mm, "end": v(-89.1, 4.14) * mm});
            skArc(sketch, "E117.MirrorCS", {"start": v(-90.61, -38.53) * mm, "mid": v(-89.85, -30.99) * mm, "end": v(-89.1, -38.53) * mm});
            skArc(sketch, "E118.MirrorCS", {"start": v(-122.36, 4.14) * mm, "mid": v(-121.6, 11.68) * mm, "end": v(-120.84, 4.14) * mm});
            skArc(sketch, "E119.MirrorCS", {"start": v(-27.11, 4.14) * mm, "mid": v(-26.35, 11.68) * mm, "end": v(-25.6, 4.14) * mm});
            skArc(sketch, "E120.MirrorCS", {"start": v(-27.11, -38.53) * mm, "mid": v(-26.35, -30.99) * mm, "end": v(-25.6, -38.53) * mm});
            skArc(sketch, "E121.MirrorCS", {"start": v(-58.86, 4.14) * mm, "mid": v(-58.1, 11.68) * mm, "end": v(-57.34, 4.14) * mm});
            skArc(sketch, "E122.MirrorCS", {"start": v(-131.64, 25.48) * mm, "mid": v(-132.4, 33.02) * mm, "end": v(-133.16, 25.48) * mm});
            skArc(sketch, "E123.MirrorCS", {"start": v(-131.64, -17.2) * mm, "mid": v(-132.4, -9.65) * mm, "end": v(-133.16, -17.2) * mm});
            skArc(sketch, "E124.MirrorCS", {"start": v(-68.14, 25.48) * mm, "mid": v(-68.9, 33.02) * mm, "end": v(-69.66, 25.48) * mm});
            skArc(sketch, "E125.MirrorCS", {"start": v(-68.14, -17.2) * mm, "mid": v(-68.9, -9.65) * mm, "end": v(-69.66, -17.2) * mm});
            skArc(sketch, "E126.MirrorCS", {"start": v(-99.89, 25.48) * mm, "mid": v(-100.65, 33.02) * mm, "end": v(-101.4, 25.48) * mm});
            skArc(sketch, "E127.MirrorCS", {"start": v(-99.89, -17.2) * mm, "mid": v(-100.65, -9.65) * mm, "end": v(-101.4, -17.2) * mm});
            skArc(sketch, "E128.MirrorCS", {"start": v(-36.39, 25.48) * mm, "mid": v(-37.15, 33.02) * mm, "end": v(-37.9, 25.48) * mm});
            skArc(sketch, "E129.MirrorCS", {"start": v(-36.39, -17.2) * mm, "mid": v(-37.15, -9.65) * mm, "end": v(-37.9, -17.2) * mm});
            skArc(sketch, "E130.MirrorCS", {"start": v(-90.61, 25.48) * mm, "mid": v(-89.85, 33.02) * mm, "end": v(-89.1, 25.48) * mm});
            skArc(sketch, "E131.MirrorCS", {"start": v(-90.61, -17.2) * mm, "mid": v(-89.85, -9.65) * mm, "end": v(-89.1, -17.2) * mm});
            skArc(sketch, "E132.MirrorCS", {"start": v(-122.36, 25.48) * mm, "mid": v(-121.6, 33.02) * mm, "end": v(-120.84, 25.48) * mm});
            skArc(sketch, "E133.MirrorCS", {"start": v(-122.36, -17.2) * mm, "mid": v(-121.6, -9.65) * mm, "end": v(-120.84, -17.2) * mm});
            skArc(sketch, "E134.MirrorCS", {"start": v(-27.11, 25.48) * mm, "mid": v(-26.35, 33.02) * mm, "end": v(-25.6, 25.48) * mm});
            skArc(sketch, "E135.MirrorCS", {"start": v(-27.11, -17.2) * mm, "mid": v(-26.35, -9.65) * mm, "end": v(-25.6, -17.2) * mm});
            skArc(sketch, "E136.MirrorCS", {"start": v(-58.86, 25.48) * mm, "mid": v(-58.1, 33.02) * mm, "end": v(-57.34, 25.48) * mm});
            skArc(sketch, "E137.MirrorCS", {"start": v(-58.86, -17.2) * mm, "mid": v(-58.1, -9.65) * mm, "end": v(-57.34, -17.2) * mm});
            skSolve(sketch);
        }
        {
            var Q0;
            Q0 = qSketchRegion(id + "F0", true);
            extrude(context, id + "F1", {"entities" : qUnion([Q0]), "depth" : 3.17 * mm});
        }
        {
            var Q0;
            Q0=makeQuery(id+"F1.opExtrude","SWEPT_FACE",FACE,{"disambiguationData":[OSD([sQuery(id+"F0.wireOp",EDGE,"E0.left")])]});
            var sketch = newSketch(context, id + "F2", { "sketchPlane" : qUnion([Q0])});
            skLineSegment(sketch, "E138.bottom", {"start": v(0, 37.47) * mm, "end": v(25.4, 37.47) * mm});
            skLineSegment(sketch, "E138.top", {"start": v(0, 40.64) * mm, "end": v(25.4, 40.64) * mm});
            skLineSegment(sketch, "E138.left", {"start": v(0, 37.47) * mm, "end": v(0, 40.64) * mm});
            skLineSegment(sketch, "E138.right", {"start": v(25.4, 37.47) * mm, "end": v(25.4, 40.64) * mm});
            skLineSegment(sketch, "E139.bottom", {"start": v(0, -50.8) * mm, "end": v(25.4, -50.8) * mm});
            skLineSegment(sketch, "E139.top", {"start": v(0, -47.62) * mm, "end": v(25.4, -47.62) * mm});
            skLineSegment(sketch, "E139.left", {"start": v(0, -50.8) * mm, "end": v(0, -47.62) * mm});
            skLineSegment(sketch, "E139.right", {"start": v(25.4, -50.8) * mm, "end": v(25.4, -47.62) * mm});
            skSolve(sketch);
        }
        {
            var Q0;
            Q0 = qSketchRegion(id + "F2", true);
            var Q1;
            Q1=makeQuery(id+"F1.opExtrude","SWEPT_FACE",FACE,{"disambiguationData":[OSD([sQuery(id+"F0.wireOp",EDGE,"E0.right")])]});
            extrude(context, id + "F3", {"entities" : qUnion([Q0]), "endBound" : BoundingType.UP_TO_SURFACE, "oppositeDirection" : true, "endBoundEntityFace" : qUnion([Q1]), "depth" : 25.4 * mm});
        }
        {
            var Q0;
            Q0=makeQuery(id+"F1.opExtrude","SWEPT_FACE",FACE,{"disambiguationData":[OSD([sQuery(id+"F0.wireOp",EDGE,"E0.left")])]});
            var sketch = newSketch(context, id + "F4", { "sketchPlane" : qUnion([Q0])});
            skLineSegment(sketch, "E140.0", {"start": v(0, 37.47) * mm, "end": v(0, -47.62) * mm});
            skLineSegment(sketch, "E141.0", {"start": v(0, 37.47) * mm, "end": v(25.4, 37.47) * mm});
            skLineSegment(sketch, "E142.0", {"start": v(0, -47.62) * mm, "end": v(25.4, -47.62) * mm});
            skPoint(sketch, "E143.0.end.orphan", {"position": v(25.4, -50.8) * mm});
            skPoint(sketch, "E143.0.start.orphan", {"position": v(0, -50.8) * mm});
            skPoint(sketch, "E144.orphan", {"position": v(0, 50.8) * mm});
            skLineSegment(sketch, "E145.bottom", {"start": v(6.7, 40.64) * mm, "end": v(18.7, 40.64) * mm});
            skLineSegment(sketch, "E145.left", {"start": v(6.7, 40.64) * mm, "end": v(6.7, 37.47) * mm});
            skLineSegment(sketch, "E145.right", {"start": v(18.7, 40.64) * mm, "end": v(18.7, 37.47) * mm});
            skPoint(sketch, "E145.middle", {"position": v(12.7, 37.47) * mm});
            skLineSegment(sketch, "E146.0", {"start": v(0, 40.64) * mm, "end": v(25.4, 40.64) * mm, "construction": true});
            skPoint(sketch, "E145.top.start.orphan", {"position": v(6.7, 34.3) * mm});
            skPoint(sketch, "E147.orphan", {"position": v(18.7, 34.3) * mm});
            skLineSegment(sketch, "E148", {"start": v(0, -5.08) * mm, "end": v(51.6, -5.08) * mm, "construction": true});
            skLineSegment(sketch, "E149.MirrorCS", {"start": v(6.7, -50.8) * mm, "end": v(6.7, -47.62) * mm});
            skLineSegment(sketch, "E150.MirrorCS", {"start": v(18.7, -50.8) * mm, "end": v(18.7, -47.62) * mm});
            skLineSegment(sketch, "E151", {"start": v(6.7, -50.8) * mm, "end": v(18.7, -50.8) * mm});
            skLineSegment(sketch, "E152", {"start": v(25.4, -47.62) * mm, "end": v(25.4, 37.47) * mm});
            skSolve(sketch);
        }
        {
            var Q0;
            Q0 = qSketchRegion(id + "F4", true);
            extrude(context, id + "F5", {"entities" : qUnion([Q0]), "oppositeDirection" : true, "depth" : 3.17 * mm});
        }
        {
            var Q0;
            Q0=makeQuery(id+"F5.opExtrude","SWEPT_BODY",BODY,{"disambiguationData":[OSD([sQuery(id+"F4.wireOp",EDGE,"E140.0"),sQuery(id+"F4.wireOp",EDGE,"E141.0"),sQuery(id+"F4.wireOp",EDGE,"E142.0"),sQuery(id+"F4.wireOp",EDGE,"E145.bottom"),sQuery(id+"F4.wireOp",EDGE,"E145.left"),sQuery(id+"F4.wireOp",EDGE,"E145.right"),sQuery(id+"F4.wireOp",EDGE,"E149.MirrorCS"),sQuery(id+"F4.wireOp",EDGE,"E150.MirrorCS"),sQuery(id+"F4.wireOp",EDGE,"E151"),sQuery(id+"F4.wireOp",EDGE,"E152")])]});
            var Q1;
            Q1=qCreatedBy(makeId("Right.planeOp"),FACE);
            mirror(context, id + "F6", {"entities" : qUnion([Q0]), "mirrorPlane" : qUnion([Q1])});
        }
        {
            var Q0;
            Q0=makeQuery(id+"F3.opExtrude","SWEPT_FACE",FACE,{"disambiguationData":[OSD([sQuery(id+"F2.wireOp",EDGE,"E138.right")])]});
            var sketch = newSketch(context, id + "F7", { "sketchPlane" : qUnion([Q0])});
            skLineSegment(sketch, "E153", {"start": v(-142.88, -6.98) * mm, "end": v(-98.43, 37.46) * mm});
            skPoint(sketch, "E154.orphan", {"position": v(-146.05, 40.64) * mm});
            skPoint(sketch, "E155.orphan", {"position": v(146.05, 40.64) * mm});
            skPoint(sketch, "E156.orphan", {"position": v(-142.88, -47.63) * mm});
            skLineSegment(sketch, "E157", {"start": v(-146.05, 40.64) * mm, "end": v(-146.05, 37.46) * mm});
            skArc(sketch, "E158", {"start": v(-136.87, 23.43) * mm, "mid": v(-131.95, 17.11) * mm, "end": v(-127.02, 23.43) * mm});
            skLineSegment(sketch, "E159", {"start": v(-136.87, 23.43) * mm, "end": v(-134.21, 33.97) * mm});
            skLineSegment(sketch, "E160", {"start": v(-132.37, 35.41) * mm, "end": v(-131.53, 35.41) * mm});
            skLineSegment(sketch, "E161", {"start": v(-129.68, 33.97) * mm, "end": v(-127.02, 23.43) * mm});
            skPoint(sketch, "E162", {"position": v(-131.95, 35.41) * mm});
            skPoint(sketch, "E163.visualSharp", {"position": v(-133.85, 35.41) * mm});
            skArc(sketch, "E163.filletArc", {"start": v(-132.37, 35.41) * mm, "mid": v(-133.54, 35.01) * mm, "end": v(-134.21, 33.97) * mm});
            skPoint(sketch, "E164.visualSharp", {"position": v(-130.04, 35.41) * mm});
            skArc(sketch, "E164.filletArc", {"start": v(-129.68, 33.97) * mm, "mid": v(-130.35, 35.01) * mm, "end": v(-131.53, 35.41) * mm});
            skArc(sketch, "E165.MirrorCS", {"start": v(136.87, 23.43) * mm, "mid": v(131.95, 17.11) * mm, "end": v(127.02, 23.43) * mm});
            skLineSegment(sketch, "E166.MirrorCS", {"start": v(136.87, 23.43) * mm, "end": v(134.21, 33.97) * mm});
            skArc(sketch, "E167.MirrorCS", {"start": v(132.37, 35.41) * mm, "mid": v(133.54, 35.01) * mm, "end": v(134.21, 33.97) * mm});
            skLineSegment(sketch, "E168.MirrorCS", {"start": v(132.37, 35.41) * mm, "end": v(131.53, 35.41) * mm});
            skArc(sketch, "E169.MirrorCS", {"start": v(129.68, 33.97) * mm, "mid": v(130.35, 35.01) * mm, "end": v(131.53, 35.41) * mm});
            skLineSegment(sketch, "E170.MirrorCS", {"start": v(129.68, 33.97) * mm, "end": v(127.02, 23.43) * mm});
            skLineSegment(sketch, "E171.MirrorCS", {"start": v(142.88, -6.98) * mm, "end": v(98.43, 37.46) * mm});
            skLineSegment(sketch, "E172.MirrorCS", {"start": v(111.13, 40.64) * mm, "end": v(130.18, 40.64) * mm});
            skLineSegment(sketch, "E173.0", {"start": v(146.05, 37.47) * mm, "end": v(98.43, 37.47) * mm});
            skLineSegment(sketch, "E174.0", {"start": v(-142.88, -6.98) * mm, "end": v(-142.88, 37.46) * mm});
            skLineSegment(sketch, "E175.trimOffspring", {"start": v(-98.43, 37.46) * mm, "end": v(-142.88, 37.46) * mm});
            skPoint(sketch, "E176.orphan", {"position": v(-146.05, 37.46) * mm});
            skPoint(sketch, "E177.0.end.orphan", {"position": v(-142.88, 40.64) * mm});
            skPoint(sketch, "E178.orphan", {"position": v(-95.25, 40.64) * mm});
            skPoint(sketch, "E179.orphan", {"position": v(-146.05, -10.16) * mm});
            skLineSegment(sketch, "E180.bottom", {"start": v(-130.18, 37.47) * mm, "end": v(-111.13, 37.47) * mm});
            skLineSegment(sketch, "E180.top", {"start": v(-130.18, 40.64) * mm, "end": v(-111.13, 40.64) * mm});
            skLineSegment(sketch, "E180.left", {"start": v(-130.18, 37.47) * mm, "end": v(-130.18, 40.64) * mm});
            skLineSegment(sketch, "E180.right", {"start": v(-111.13, 37.46) * mm, "end": v(-111.13, 40.64) * mm});
            skLineSegment(sketch, "E181.bottom", {"start": v(-142.88, 24.76) * mm, "end": v(-146.05, 24.76) * mm});
            skLineSegment(sketch, "E181.top", {"start": v(-142.88, 5.72) * mm, "end": v(-146.05, 5.72) * mm});
            skLineSegment(sketch, "E181.left", {"start": v(-142.88, 24.76) * mm, "end": v(-142.88, 5.72) * mm});
            skLineSegment(sketch, "E181.right", {"start": v(-146.05, 24.76) * mm, "end": v(-146.05, 5.72) * mm});
            skLineSegment(sketch, "E182.MirrorCS", {"start": v(142.88, 5.72) * mm, "end": v(146.05, 5.72) * mm});
            skLineSegment(sketch, "E183.MirrorCS", {"start": v(146.05, 24.76) * mm, "end": v(146.05, 5.72) * mm});
            skLineSegment(sketch, "E184.MirrorCS", {"start": v(142.88, 24.76) * mm, "end": v(146.05, 24.76) * mm});
            skLineSegment(sketch, "E185.MirrorCS", {"start": v(130.18, 37.47) * mm, "end": v(130.18, 40.64) * mm});
            skLineSegment(sketch, "E186.MirrorCS", {"start": v(130.18, 40.64) * mm, "end": v(111.13, 40.64) * mm});
            skLineSegment(sketch, "E187.MirrorCS", {"start": v(111.13, 37.46) * mm, "end": v(111.13, 40.64) * mm});
            skPoint(sketch, "E188.orphan", {"position": v(95.25, 40.64) * mm});
            skPoint(sketch, "E189.MirrorCS.start.orphan", {"position": v(142.88, 40.64) * mm});
            skLineSegment(sketch, "E190", {"start": v(142.88, 5.72) * mm, "end": v(142.88, -6.98) * mm});
            skLineSegment(sketch, "E191", {"start": v(142.88, 24.76) * mm, "end": v(142.88, 37.47) * mm});
            skPoint(sketch, "E192.orphan", {"position": v(146.05, -10.16) * mm});
            skSolve(sketch);
        }
        {
            var Q0;
            Q0 = qSketchRegion(id + "F7", true);
            extrude(context, id + "F8", {"entities" : qUnion([Q0]), "oppositeDirection" : true, "depth" : 3.17 * mm});
        }
        {
            var Q0;
            Q0=makeQuery(id+"F5.opExtrude","CAP_FACE",FACE,{"disambiguationData":[OSD([sQuery(id+"F4.wireOp",EDGE,"E140.0"),sQuery(id+"F4.wireOp",EDGE,"E141.0"),sQuery(id+"F4.wireOp",EDGE,"E142.0"),sQuery(id+"F4.wireOp",EDGE,"E145.bottom"),sQuery(id+"F4.wireOp",EDGE,"E145.left"),sQuery(id+"F4.wireOp",EDGE,"E145.right"),sQuery(id+"F4.wireOp",EDGE,"E149.MirrorCS"),sQuery(id+"F4.wireOp",EDGE,"E150.MirrorCS"),sQuery(id+"F4.wireOp",EDGE,"E151"),sQuery(id+"F4.wireOp",EDGE,"E152")])],"isStart":true});
            var sketch = newSketch(context, id + "F9", { "sketchPlane" : qUnion([Q0])});
            skLineSegment(sketch, "E193.0", {"start": v(22.23, 24.76) * mm, "end": v(22.23, 5.72) * mm, "construction": true});
            skLineSegment(sketch, "E194.0", {"start": v(22.23, 24.76) * mm, "end": v(25.4, 24.76) * mm, "construction": true});
            skLineSegment(sketch, "E195.0", {"start": v(22.23, 5.72) * mm, "end": v(25.4, 5.72) * mm, "construction": true});
            skLineSegment(sketch, "E196.0", {"start": v(6.7, 40.64) * mm, "end": v(6.7, 37.47) * mm, "construction": true});
            skLineSegment(sketch, "E197.0", {"start": v(18.7, 40.64) * mm, "end": v(18.7, 37.47) * mm, "construction": true});
            skLineSegment(sketch, "E198.0", {"start": v(6.7, -50.8) * mm, "end": v(6.7, -47.62) * mm, "construction": true});
            skLineSegment(sketch, "E199.0", {"start": v(18.7, -50.8) * mm, "end": v(18.7, -47.62) * mm, "construction": true});
            skLineSegment(sketch, "E200", {"start": v(6.66, 40.64) * mm, "end": v(6.66, 37.47) * mm});
            skPoint(sketch, "E200.startSnap0", {"position": v(12.7, 40.64) * mm});
            skLineSegment(sketch, "E201", {"start": v(18.75, 40.64) * mm, "end": v(18.74, 37.47) * mm});
            skLineSegment(sketch, "E202", {"start": v(6.66, 40.64) * mm, "end": v(18.75, 40.64) * mm});
            skLineSegment(sketch, "E203", {"start": v(6.66, 37.47) * mm, "end": v(18.74, 37.47) * mm});
            skLineSegment(sketch, "E204.bottom", {"start": v(25.4, 24.8) * mm, "end": v(22.23, 24.8) * mm});
            skLineSegment(sketch, "E204.top", {"start": v(25.4, 5.7) * mm, "end": v(22.23, 5.7) * mm});
            skLineSegment(sketch, "E204.left", {"start": v(25.4, 24.8) * mm, "end": v(25.4, 5.7) * mm});
            skLineSegment(sketch, "E204.right", {"start": v(22.23, 24.8) * mm, "end": v(22.23, 5.7) * mm});
            skLineSegment(sketch, "E205.bottom", {"start": v(6.63, -47.62) * mm, "end": v(18.77, -47.62) * mm});
            skLineSegment(sketch, "E205.top", {"start": v(6.63, -50.8) * mm, "end": v(18.77, -50.8) * mm});
            skLineSegment(sketch, "E205.left", {"start": v(6.63, -47.62) * mm, "end": v(6.63, -50.8) * mm});
            skLineSegment(sketch, "E205.right", {"start": v(18.77, -47.62) * mm, "end": v(18.77, -50.8) * mm});
            skSolve(sketch);
        }
        {
            var Q0;
            Q0 = qSketchRegion(id + "F9", true);
            extrude(context, id + "F10", {"entities" : qUnion([Q0]), "operationType" : NewBodyOperationType.REMOVE, "oppositeDirection" : true, "depth" : 3.17 * mm});
        }
        {
            var Q0;
            Q0=makeQuery(id+"F5.opExtrude","CAP_FACE",FACE,{"disambiguationData":[OSD([sQuery(id+"F4.wireOp",EDGE,"E140.0"),sQuery(id+"F4.wireOp",EDGE,"E141.0"),sQuery(id+"F4.wireOp",EDGE,"E142.0"),sQuery(id+"F4.wireOp",EDGE,"E145.bottom"),sQuery(id+"F4.wireOp",EDGE,"E145.left"),sQuery(id+"F4.wireOp",EDGE,"E145.right"),sQuery(id+"F4.wireOp",EDGE,"E149.MirrorCS"),sQuery(id+"F4.wireOp",EDGE,"E150.MirrorCS"),sQuery(id+"F4.wireOp",EDGE,"E151"),sQuery(id+"F4.wireOp",EDGE,"E152")])],"isStart":true});
            var sketch = newSketch(context, id + "F11", { "sketchPlane" : qUnion([Q0])});
            skLineSegment(sketch, "E206.bottom", {"start": v(25.4, 24.8) * mm, "end": v(22.23, 24.8) * mm});
            skLineSegment(sketch, "E206.top", {"start": v(25.4, 5.68) * mm, "end": v(22.23, 5.68) * mm});
            skLineSegment(sketch, "E206.left", {"start": v(25.4, 24.8) * mm, "end": v(25.4, 5.68) * mm});
            skLineSegment(sketch, "E206.right", {"start": v(22.23, 24.8) * mm, "end": v(22.23, 5.68) * mm});
            skSolve(sketch);
        }
        {
            var Q0;
            Q0 = qSketchRegion(id + "F11", true);
            var Q1;
            Q1=makeQuery(id+"F6.opPattern","COPY",FACE,{"derivedFrom":makeQuery(id+"F5.opExtrude","CAP_FACE",FACE,{"disambiguationData":[OSD([sQuery(id+"F4.wireOp",EDGE,"E140.0"),sQuery(id+"F4.wireOp",EDGE,"E141.0"),sQuery(id+"F4.wireOp",EDGE,"E142.0"),sQuery(id+"F4.wireOp",EDGE,"E145.bottom"),sQuery(id+"F4.wireOp",EDGE,"E145.left"),sQuery(id+"F4.wireOp",EDGE,"E145.right"),sQuery(id+"F4.wireOp",EDGE,"E149.MirrorCS"),sQuery(id+"F4.wireOp",EDGE,"E150.MirrorCS"),sQuery(id+"F4.wireOp",EDGE,"E151"),sQuery(id+"F4.wireOp",EDGE,"E152")])],"isStart":true}),"instanceName":"1"});
            var Q2;
            Q2=makeQuery(id+"F6.opPattern","COPY",FACE,{"derivedFrom":makeQuery(id+"F5.opExtrude","CAP_FACE",FACE,{"disambiguationData":[OSD([sQuery(id+"F4.wireOp",EDGE,"E140.0"),sQuery(id+"F4.wireOp",EDGE,"E141.0"),sQuery(id+"F4.wireOp",EDGE,"E142.0"),sQuery(id+"F4.wireOp",EDGE,"E145.bottom"),sQuery(id+"F4.wireOp",EDGE,"E145.left"),sQuery(id+"F4.wireOp",EDGE,"E145.right"),sQuery(id+"F4.wireOp",EDGE,"E149.MirrorCS"),sQuery(id+"F4.wireOp",EDGE,"E150.MirrorCS"),sQuery(id+"F4.wireOp",EDGE,"E151"),sQuery(id+"F4.wireOp",EDGE,"E152")])],"isStart":true}),"instanceName":"1"});
            extrude(context, id + "F12", {"entities" : qUnion([Q0]), "operationType" : NewBodyOperationType.REMOVE, "endBound" : BoundingType.UP_TO_SURFACE, "oppositeDirection" : true, "endBoundEntityFace" : qUnion([Q1]), "depth" : 25.4 * mm});
        }
        {
            var Q0;
            Q0=makeQuery(id+"F3.opExtrude","SWEPT_FACE",FACE,{"disambiguationData":[OSD([sQuery(id+"F2.wireOp",EDGE,"E138.top")])]});
            var sketch = newSketch(context, id + "F13", { "sketchPlane" : qUnion([Q0])});
            skLineSegment(sketch, "E207.0", {"start": v(-146.05, 25.4) * mm, "end": v(-146.05, 22.23) * mm, "construction": true});
            skLineSegment(sketch, "E208.0", {"start": v(-146.05, 25.4) * mm, "end": v(146.05, 25.4) * mm, "construction": true});
            skLineSegment(sketch, "E209.0", {"start": v(146.05, 18.75) * mm, "end": v(146.05, 25.4) * mm, "construction": true});
            skLineSegment(sketch, "E210.bottom", {"start": v(146.05, 18.78) * mm, "end": v(142.88, 18.78) * mm});
            skLineSegment(sketch, "E210.top", {"start": v(146.05, 6.63) * mm, "end": v(142.88, 6.63) * mm});
            skLineSegment(sketch, "E210.left", {"start": v(146.05, 18.78) * mm, "end": v(146.05, 6.63) * mm});
            skLineSegment(sketch, "E210.right", {"start": v(142.88, 18.78) * mm, "end": v(142.88, 6.63) * mm});
            skLineSegment(sketch, "E211.bottom", {"start": v(111.09, 25.4) * mm, "end": v(130.21, 25.4) * mm});
            skLineSegment(sketch, "E211.top", {"start": v(111.09, 22.23) * mm, "end": v(130.21, 22.23) * mm});
            skLineSegment(sketch, "E211.left", {"start": v(111.09, 25.4) * mm, "end": v(111.09, 22.23) * mm});
            skLineSegment(sketch, "E211.right", {"start": v(130.21, 25.4) * mm, "end": v(130.21, 22.23) * mm});
            skLineSegment(sketch, "E212.bottom", {"start": v(-130.21, 25.4) * mm, "end": v(-111.09, 25.4) * mm});
            skLineSegment(sketch, "E212.top", {"start": v(-130.21, 22.23) * mm, "end": v(-111.09, 22.23) * mm});
            skLineSegment(sketch, "E212.left", {"start": v(-130.21, 25.4) * mm, "end": v(-130.21, 22.22) * mm});
            skLineSegment(sketch, "E212.right", {"start": v(-111.09, 25.4) * mm, "end": v(-111.09, 22.23) * mm});
            skLineSegment(sketch, "E213.top", {"start": v(-146.05, 6.63) * mm, "end": v(-142.88, 6.63) * mm});
            skLineSegment(sketch, "E213.left", {"start": v(-146.05, 18.77) * mm, "end": v(-146.05, 6.63) * mm});
            skLineSegment(sketch, "E213.right", {"start": v(-142.88, 18.77) * mm, "end": v(-142.88, 6.63) * mm});
            skLineSegment(sketch, "E214", {"start": v(-146.05, 18.77) * mm, "end": v(-142.88, 18.77) * mm});
            skPoint(sketch, "E215.orphan", {"position": v(-142.88, 24.4) * mm});
            skLineSegment(sketch, "E216.trimOffspring", {"start": v(-146.05, 18.77) * mm, "end": v(-146.05, 0) * mm, "construction": true});
            skSolve(sketch);
        }
        {
            var Q0;
            Q0 = qSketchRegion(id + "F13", true);
            extrude(context, id + "F14", {"entities" : qUnion([Q0]), "operationType" : NewBodyOperationType.REMOVE, "endBound" : BoundingType.THROUGH_ALL, "oppositeDirection" : true, "depth" : 25.4 * mm});
        }
        {
            var Q0;
            Q0=makeQuery(id+"F1.opExtrude","SWEPT_EDGE",EDGE,{"disambiguationData":[OSD([sQuery(id+"F0.wireOp",EDGE,"E0.bottom"),sQuery(id+"F0.wireOp",EDGE,"E0.right")])]});
            var Q1;
            Q1=makeQuery(id+"F1.opExtrude","SWEPT_EDGE",EDGE,{"disambiguationData":[OSD([sQuery(id+"F0.wireOp",EDGE,"E0.bottom"),sQuery(id+"F0.wireOp",EDGE,"E0.left")])]});
            fillet(context, id + "F15", {"entities" : qUnion([Q0, Q1]), "radius" : 7.62 * mm, "tangentPropagation" : true, "allowEdgeOverflow" : false});
        }
        {
            var Q0;
            Q0=makeQuery(id+"F1.opExtrude","SWEPT_EDGE",EDGE,{"disambiguationData":[OSD([sQuery(id+"F0.wireOp",EDGE,"E47.MirrorCS"),sQuery(id+"F0.wireOp",EDGE,"E122.MirrorCS")])]});
            var Q1;
            Q1=makeQuery(id+"F1.opExtrude","SWEPT_EDGE",EDGE,{"disambiguationData":[OSD([sQuery(id+"F0.wireOp",EDGE,"E51.MirrorCS"),sQuery(id+"F0.wireOp",EDGE,"E122.MirrorCS")])]});
            var Q2;
            Q2=makeQuery(id+"F1.opExtrude","SWEPT_EDGE",EDGE,{"disambiguationData":[OSD([sQuery(id+"F0.wireOp",EDGE,"E74.MirrorCS"),sQuery(id+"F0.wireOp",EDGE,"E132.MirrorCS")])]});
            var Q3;
            Q3=makeQuery(id+"F1.opExtrude","SWEPT_EDGE",EDGE,{"disambiguationData":[OSD([sQuery(id+"F0.wireOp",EDGE,"E97.MirrorCS"),sQuery(id+"F0.wireOp",EDGE,"E110.MirrorCS")])]});
            var Q4;
            Q4=makeQuery(id+"F1.opExtrude","SWEPT_EDGE",EDGE,{"disambiguationData":[OSD([sQuery(id+"F0.wireOp",EDGE,"E31.MirrorCS"),sQuery(id+"F0.wireOp",EDGE,"E118.MirrorCS")])]});
            var Q5;
            Q5=makeQuery(id+"F1.opExtrude","SWEPT_EDGE",EDGE,{"disambiguationData":[OSD([sQuery(id+"F0.wireOp",EDGE,"E45.MirrorCS"),sQuery(id+"F0.wireOp",EDGE,"E126.MirrorCS")])]});
            var Q6;
            Q6=makeQuery(id+"F1.opExtrude","SWEPT_EDGE",EDGE,{"disambiguationData":[OSD([sQuery(id+"F0.wireOp",EDGE,"E78.MirrorCS"),sQuery(id+"F0.wireOp",EDGE,"E130.MirrorCS")])]});
            var Q7;
            Q7=makeQuery(id+"F1.opExtrude","SWEPT_EDGE",EDGE,{"disambiguationData":[OSD([sQuery(id+"F0.wireOp",EDGE,"E95.MirrorCS"),sQuery(id+"F0.wireOp",EDGE,"E108.MirrorCS")])]});
            var Q8;
            Q8=makeQuery(id+"F1.opExtrude","SWEPT_EDGE",EDGE,{"disambiguationData":[OSD([sQuery(id+"F0.wireOp",EDGE,"E29.MirrorCS"),sQuery(id+"F0.wireOp",EDGE,"E116.MirrorCS")])]});
            var Q9;
            Q9=makeQuery(id+"F1.opExtrude","SWEPT_EDGE",EDGE,{"disambiguationData":[OSD([sQuery(id+"F0.wireOp",EDGE,"E50.MirrorCS"),sQuery(id+"F0.wireOp",EDGE,"E124.MirrorCS")])]});
            var Q10;
            Q10=makeQuery(id+"F1.opExtrude","SWEPT_EDGE",EDGE,{"disambiguationData":[OSD([sQuery(id+"F0.wireOp",EDGE,"E101.MirrorCS"),sQuery(id+"F0.wireOp",EDGE,"E113.MirrorCS")])]});
            var Q11;
            Q11=makeQuery(id+"F1.opExtrude","SWEPT_EDGE",EDGE,{"disambiguationData":[OSD([sQuery(id+"F0.wireOp",EDGE,"E76.MirrorCS"),sQuery(id+"F0.wireOp",EDGE,"E136.MirrorCS")])]});
            var Q12;
            Q12=makeQuery(id+"F1.opExtrude","SWEPT_EDGE",EDGE,{"disambiguationData":[OSD([sQuery(id+"F0.wireOp",EDGE,"E34.MirrorCS"),sQuery(id+"F0.wireOp",EDGE,"E121.MirrorCS")])]});
            var Q13;
            Q13=makeQuery(id+"F1.opExtrude","SWEPT_EDGE",EDGE,{"disambiguationData":[OSD([sQuery(id+"F0.wireOp",EDGE,"E44.MirrorCS"),sQuery(id+"F0.wireOp",EDGE,"E125.MirrorCS")])]});
            var Q14;
            Q14=makeQuery(id+"F1.opExtrude","SWEPT_EDGE",EDGE,{"disambiguationData":[OSD([sQuery(id+"F0.wireOp",EDGE,"E79.MirrorCS"),sQuery(id+"F0.wireOp",EDGE,"E131.MirrorCS")])]});
            var Q15;
            Q15=makeQuery(id+"F1.opExtrude","SWEPT_EDGE",EDGE,{"disambiguationData":[OSD([sQuery(id+"F0.wireOp",EDGE,"E46.MirrorCS"),sQuery(id+"F0.wireOp",EDGE,"E127.MirrorCS")])]});
            var Q16;
            Q16=makeQuery(id+"F1.opExtrude","SWEPT_EDGE",EDGE,{"disambiguationData":[OSD([sQuery(id+"F0.wireOp",EDGE,"E75.MirrorCS"),sQuery(id+"F0.wireOp",EDGE,"E133.MirrorCS")])]});
            var Q17;
            Q17=makeQuery(id+"F1.opExtrude","SWEPT_EDGE",EDGE,{"disambiguationData":[OSD([sQuery(id+"F0.wireOp",EDGE,"E43.MirrorCS"),sQuery(id+"F0.wireOp",EDGE,"E123.MirrorCS")])]});
            var Q18;
            Q18=makeQuery(id+"F1.opExtrude","SWEPT_EDGE",EDGE,{"disambiguationData":[OSD([sQuery(id+"F0.wireOp",EDGE,"E77.MirrorCS"),sQuery(id+"F0.wireOp",EDGE,"E137.MirrorCS")])]});
            var Q19;
            Q19=makeQuery(id+"F1.opExtrude","SWEPT_EDGE",EDGE,{"disambiguationData":[OSD([sQuery(id+"F0.wireOp",EDGE,"E99.MirrorCS"),sQuery(id+"F0.wireOp",EDGE,"E111.MirrorCS")])]});
            var Q20;
            Q20=makeQuery(id+"F1.opExtrude","SWEPT_EDGE",EDGE,{"disambiguationData":[OSD([sQuery(id+"F0.wireOp",EDGE,"E48.MirrorCS"),sQuery(id+"F0.wireOp",EDGE,"E128.MirrorCS")])]});
            var Q21;
            Q21=makeQuery(id+"F1.opExtrude","SWEPT_EDGE",EDGE,{"disambiguationData":[OSD([sQuery(id+"F0.wireOp",EDGE,"E32.MirrorCS"),sQuery(id+"F0.wireOp",EDGE,"E119.MirrorCS")])]});
            var Q22;
            Q22=makeQuery(id+"F1.opExtrude","SWEPT_EDGE",EDGE,{"disambiguationData":[OSD([sQuery(id+"F0.wireOp",EDGE,"E80.MirrorCS"),sQuery(id+"F0.wireOp",EDGE,"E134.MirrorCS")])]});
            var Q23;
            Q23=makeQuery(id+"F1.opExtrude","SWEPT_EDGE",EDGE,{"disambiguationData":[OSD([sQuery(id+"F0.wireOp",EDGE,"E2"),sQuery(id+"F0.wireOp",EDGE,"E3.right")])]});
            var Q24;
            Q24=makeQuery(id+"F1.opExtrude","SWEPT_EDGE",EDGE,{"disambiguationData":[OSD([sQuery(id+"F0.wireOp",EDGE,"E6.MirrorCS"),sQuery(id+"F0.wireOp",EDGE,"E8.MirrorCS")])]});
            var Q25;
            Q25=makeQuery(id+"F1.opExtrude","SWEPT_EDGE",EDGE,{"disambiguationData":[OSD([sQuery(id+"F0.wireOp",EDGE,"E9.0.1.0"),sQuery(id+"F0.wireOp",EDGE,"E9.0.1.3")])]});
            var Q26;
            Q26=makeQuery(id+"F1.opExtrude","SWEPT_EDGE",EDGE,{"disambiguationData":[OSD([sQuery(id+"F0.wireOp",EDGE,"E9.0.1.4"),sQuery(id+"F0.wireOp",EDGE,"E9.0.1.5")])]});
            var Q27;
            Q27=makeQuery(id+"F1.opExtrude","SWEPT_EDGE",EDGE,{"disambiguationData":[OSD([sQuery(id+"F0.wireOp",EDGE,"E9.1.1.0"),sQuery(id+"F0.wireOp",EDGE,"E9.1.1.3")])]});
            var Q28;
            Q28=makeQuery(id+"F1.opExtrude","SWEPT_EDGE",EDGE,{"disambiguationData":[OSD([sQuery(id+"F0.wireOp",EDGE,"E9.1.0.0"),sQuery(id+"F0.wireOp",EDGE,"E9.1.0.3")])]});
            var Q29;
            Q29=makeQuery(id+"F1.opExtrude","SWEPT_EDGE",EDGE,{"disambiguationData":[OSD([sQuery(id+"F0.wireOp",EDGE,"E9.1.0.4"),sQuery(id+"F0.wireOp",EDGE,"E9.1.0.5")])]});
            var Q30;
            Q30=makeQuery(id+"F1.opExtrude","SWEPT_EDGE",EDGE,{"disambiguationData":[OSD([sQuery(id+"F0.wireOp",EDGE,"E9.1.1.4"),sQuery(id+"F0.wireOp",EDGE,"E9.1.1.5")])]});
            var Q31;
            Q31=makeQuery(id+"F1.opExtrude","SWEPT_EDGE",EDGE,{"disambiguationData":[OSD([sQuery(id+"F0.wireOp",EDGE,"E9.2.0.0"),sQuery(id+"F0.wireOp",EDGE,"E9.2.0.3")])]});
            var Q32;
            Q32=makeQuery(id+"F1.opExtrude","SWEPT_EDGE",EDGE,{"disambiguationData":[OSD([sQuery(id+"F0.wireOp",EDGE,"E9.2.0.4"),sQuery(id+"F0.wireOp",EDGE,"E9.2.0.5")])]});
            var Q33;
            Q33=makeQuery(id+"F1.opExtrude","SWEPT_EDGE",EDGE,{"disambiguationData":[OSD([sQuery(id+"F0.wireOp",EDGE,"E9.2.1.0"),sQuery(id+"F0.wireOp",EDGE,"E9.2.1.3")])]});
            var Q34;
            Q34=makeQuery(id+"F1.opExtrude","SWEPT_EDGE",EDGE,{"disambiguationData":[OSD([sQuery(id+"F0.wireOp",EDGE,"E9.2.1.4"),sQuery(id+"F0.wireOp",EDGE,"E9.2.1.5")])]});
            var Q35;
            Q35=makeQuery(id+"F1.opExtrude","SWEPT_EDGE",EDGE,{"disambiguationData":[OSD([sQuery(id+"F0.wireOp",EDGE,"E9.3.1.0"),sQuery(id+"F0.wireOp",EDGE,"E9.3.1.3")])]});
            var Q36;
            Q36=makeQuery(id+"F1.opExtrude","SWEPT_EDGE",EDGE,{"disambiguationData":[OSD([sQuery(id+"F0.wireOp",EDGE,"E9.3.0.0"),sQuery(id+"F0.wireOp",EDGE,"E9.3.0.3")])]});
            var Q37;
            Q37=makeQuery(id+"F1.opExtrude","SWEPT_EDGE",EDGE,{"disambiguationData":[OSD([sQuery(id+"F0.wireOp",EDGE,"E9.3.0.4"),sQuery(id+"F0.wireOp",EDGE,"E9.3.0.5")])]});
            var Q38;
            Q38=makeQuery(id+"F1.opExtrude","SWEPT_EDGE",EDGE,{"disambiguationData":[OSD([sQuery(id+"F0.wireOp",EDGE,"E9.3.1.4"),sQuery(id+"F0.wireOp",EDGE,"E9.3.1.5")])]});
            var Q39;
            Q39=makeQuery(id+"F1.opExtrude","SWEPT_EDGE",EDGE,{"disambiguationData":[OSD([sQuery(id+"F0.wireOp",EDGE,"E9.4.1.0"),sQuery(id+"F0.wireOp",EDGE,"E9.4.1.3")])]});
            var Q40;
            Q40=makeQuery(id+"F1.opExtrude","SWEPT_EDGE",EDGE,{"disambiguationData":[OSD([sQuery(id+"F0.wireOp",EDGE,"E9.4.1.4"),sQuery(id+"F0.wireOp",EDGE,"E9.4.1.5")])]});
            var Q41;
            Q41=makeQuery(id+"F1.opExtrude","SWEPT_EDGE",EDGE,{"disambiguationData":[OSD([sQuery(id+"F0.wireOp",EDGE,"E9.4.0.4"),sQuery(id+"F0.wireOp",EDGE,"E9.4.0.5")])]});
            var Q42;
            Q42=makeQuery(id+"F1.opExtrude","SWEPT_EDGE",EDGE,{"disambiguationData":[OSD([sQuery(id+"F0.wireOp",EDGE,"E9.4.0.0"),sQuery(id+"F0.wireOp",EDGE,"E9.4.0.3")])]});
            var Q43;
            Q43=makeQuery(id+"F1.opExtrude","SWEPT_EDGE",EDGE,{"disambiguationData":[OSD([sQuery(id+"F0.wireOp",EDGE,"E9.3.3.4"),sQuery(id+"F0.wireOp",EDGE,"E9.3.3.5")])]});
            var Q44;
            Q44=makeQuery(id+"F1.opExtrude","SWEPT_EDGE",EDGE,{"disambiguationData":[OSD([sQuery(id+"F0.wireOp",EDGE,"E9.3.3.0"),sQuery(id+"F0.wireOp",EDGE,"E9.3.3.3")])]});
            var Q45;
            Q45=makeQuery(id+"F1.opExtrude","SWEPT_EDGE",EDGE,{"disambiguationData":[OSD([sQuery(id+"F0.wireOp",EDGE,"E9.4.3.0"),sQuery(id+"F0.wireOp",EDGE,"E9.4.3.3")])]});
            var Q46;
            Q46=makeQuery(id+"F1.opExtrude","SWEPT_EDGE",EDGE,{"disambiguationData":[OSD([sQuery(id+"F0.wireOp",EDGE,"E9.4.3.4"),sQuery(id+"F0.wireOp",EDGE,"E9.4.3.5")])]});
            var Q47;
            Q47=makeQuery(id+"F1.opExtrude","SWEPT_EDGE",EDGE,{"disambiguationData":[OSD([sQuery(id+"F0.wireOp",EDGE,"E9.4.2.4"),sQuery(id+"F0.wireOp",EDGE,"E9.4.2.5")])]});
            var Q48;
            Q48=makeQuery(id+"F1.opExtrude","SWEPT_EDGE",EDGE,{"disambiguationData":[OSD([sQuery(id+"F0.wireOp",EDGE,"E9.4.2.0"),sQuery(id+"F0.wireOp",EDGE,"E9.4.2.3")])]});
            var Q49;
            Q49=makeQuery(id+"F1.opExtrude","SWEPT_EDGE",EDGE,{"disambiguationData":[OSD([sQuery(id+"F0.wireOp",EDGE,"E9.3.2.4"),sQuery(id+"F0.wireOp",EDGE,"E9.3.2.5")])]});
            var Q50;
            Q50=makeQuery(id+"F1.opExtrude","SWEPT_EDGE",EDGE,{"disambiguationData":[OSD([sQuery(id+"F0.wireOp",EDGE,"E9.3.2.0"),sQuery(id+"F0.wireOp",EDGE,"E9.3.2.3")])]});
            var Q51;
            Q51=makeQuery(id+"F1.opExtrude","SWEPT_EDGE",EDGE,{"disambiguationData":[OSD([sQuery(id+"F0.wireOp",EDGE,"E9.2.2.0"),sQuery(id+"F0.wireOp",EDGE,"E9.2.2.3")])]});
            var Q52;
            Q52=makeQuery(id+"F1.opExtrude","SWEPT_EDGE",EDGE,{"disambiguationData":[OSD([sQuery(id+"F0.wireOp",EDGE,"E9.2.3.4"),sQuery(id+"F0.wireOp",EDGE,"E9.2.3.5")])]});
            var Q53;
            Q53=makeQuery(id+"F1.opExtrude","SWEPT_EDGE",EDGE,{"disambiguationData":[OSD([sQuery(id+"F0.wireOp",EDGE,"E9.2.2.4"),sQuery(id+"F0.wireOp",EDGE,"E9.2.2.5")])]});
            var Q54;
            Q54=makeQuery(id+"F1.opExtrude","SWEPT_EDGE",EDGE,{"disambiguationData":[OSD([sQuery(id+"F0.wireOp",EDGE,"E9.2.3.0"),sQuery(id+"F0.wireOp",EDGE,"E9.2.3.3")])]});
            var Q55;
            Q55=makeQuery(id+"F1.opExtrude","SWEPT_EDGE",EDGE,{"disambiguationData":[OSD([sQuery(id+"F0.wireOp",EDGE,"E9.1.3.4"),sQuery(id+"F0.wireOp",EDGE,"E9.1.3.5")])]});
            var Q56;
            Q56=makeQuery(id+"F1.opExtrude","SWEPT_EDGE",EDGE,{"disambiguationData":[OSD([sQuery(id+"F0.wireOp",EDGE,"E9.1.2.0"),sQuery(id+"F0.wireOp",EDGE,"E9.1.2.3")])]});
            var Q57;
            Q57=makeQuery(id+"F1.opExtrude","SWEPT_EDGE",EDGE,{"disambiguationData":[OSD([sQuery(id+"F0.wireOp",EDGE,"E9.1.2.4"),sQuery(id+"F0.wireOp",EDGE,"E9.1.2.5")])]});
            var Q58;
            Q58=makeQuery(id+"F1.opExtrude","SWEPT_EDGE",EDGE,{"disambiguationData":[OSD([sQuery(id+"F0.wireOp",EDGE,"E9.0.2.4"),sQuery(id+"F0.wireOp",EDGE,"E9.0.2.5")])]});
            var Q59;
            Q59=makeQuery(id+"F1.opExtrude","SWEPT_EDGE",EDGE,{"disambiguationData":[OSD([sQuery(id+"F0.wireOp",EDGE,"E9.0.3.0"),sQuery(id+"F0.wireOp",EDGE,"E9.0.3.3")])]});
            var Q60;
            Q60=makeQuery(id+"F1.opExtrude","SWEPT_EDGE",EDGE,{"disambiguationData":[OSD([sQuery(id+"F0.wireOp",EDGE,"E9.0.3.4"),sQuery(id+"F0.wireOp",EDGE,"E9.0.3.5")])]});
            var Q61;
            Q61=makeQuery(id+"F1.opExtrude","SWEPT_EDGE",EDGE,{"disambiguationData":[OSD([sQuery(id+"F0.wireOp",EDGE,"E9.1.3.0"),sQuery(id+"F0.wireOp",EDGE,"E9.1.3.3")])]});
            var Q62;
            Q62=makeQuery(id+"F1.opExtrude","SWEPT_EDGE",EDGE,{"disambiguationData":[OSD([sQuery(id+"F0.wireOp",EDGE,"E96.MirrorCS"),sQuery(id+"F0.wireOp",EDGE,"E112.MirrorCS")])]});
            var Q63;
            Q63=makeQuery(id+"F1.opExtrude","SWEPT_EDGE",EDGE,{"disambiguationData":[OSD([sQuery(id+"F0.wireOp",EDGE,"E33.MirrorCS"),sQuery(id+"F0.wireOp",EDGE,"E120.MirrorCS")])]});
            var Q64;
            Q64=makeQuery(id+"F1.opExtrude","SWEPT_EDGE",EDGE,{"disambiguationData":[OSD([sQuery(id+"F0.wireOp",EDGE,"E81.MirrorCS"),sQuery(id+"F0.wireOp",EDGE,"E135.MirrorCS")])]});
            var Q65;
            Q65=makeQuery(id+"F1.opExtrude","SWEPT_EDGE",EDGE,{"disambiguationData":[OSD([sQuery(id+"F0.wireOp",EDGE,"E49.MirrorCS"),sQuery(id+"F0.wireOp",EDGE,"E129.MirrorCS")])]});
            var Q66;
            Q66=makeQuery(id+"F1.opExtrude","SWEPT_EDGE",EDGE,{"disambiguationData":[OSD([sQuery(id+"F0.wireOp",EDGE,"E28.MirrorCS"),sQuery(id+"F0.wireOp",EDGE,"E115.MirrorCS")])]});
            var Q67;
            Q67=makeQuery(id+"F1.opExtrude","SWEPT_EDGE",EDGE,{"disambiguationData":[OSD([sQuery(id+"F0.wireOp",EDGE,"E90.MirrorCS"),sQuery(id+"F0.wireOp",EDGE,"E107.MirrorCS")])]});
            var Q68;
            Q68=makeQuery(id+"F1.opExtrude","SWEPT_EDGE",EDGE,{"disambiguationData":[OSD([sQuery(id+"F0.wireOp",EDGE,"E30.MirrorCS"),sQuery(id+"F0.wireOp",EDGE,"E117.MirrorCS")])]});
            var Q69;
            Q69=makeQuery(id+"F1.opExtrude","SWEPT_EDGE",EDGE,{"disambiguationData":[OSD([sQuery(id+"F0.wireOp",EDGE,"E102.MirrorCS"),sQuery(id+"F0.wireOp",EDGE,"E109.MirrorCS")])]});
            var Q70;
            Q70=makeQuery(id+"F1.opExtrude","SWEPT_EDGE",EDGE,{"disambiguationData":[OSD([sQuery(id+"F0.wireOp",EDGE,"E103.MirrorCS"),sQuery(id+"F0.wireOp",EDGE,"E106.MirrorCS")])]});
            var Q71;
            Q71=makeQuery(id+"F1.opExtrude","SWEPT_EDGE",EDGE,{"disambiguationData":[OSD([sQuery(id+"F0.wireOp",EDGE,"E27.MirrorCS"),sQuery(id+"F0.wireOp",EDGE,"E114.MirrorCS")])]});
            var Q72;
            Q72=makeQuery(id+"F1.opExtrude","SWEPT_EDGE",EDGE,{"disambiguationData":[OSD([sQuery(id+"F0.wireOp",EDGE,"E9.0.2.0"),sQuery(id+"F0.wireOp",EDGE,"E9.0.2.3")])]});
            chamfer(context, id + "F16", {"entities" : qUnion([Q0, Q1, Q2, Q3, Q4, Q5, Q6, Q7, Q8, Q9, Q10, Q11, Q12, Q13, Q14, Q15, Q16, Q17, Q18, Q19, Q20, Q21, Q22, Q23, Q24, Q25, Q26, Q27, Q28, Q29, Q30, Q31, Q32, Q33, Q34, Q35, Q36, Q37, Q38, Q39, Q40, Q41, Q42, Q43, Q44, Q45, Q46, Q47, Q48, Q49, Q50, Q51, Q52, Q53, Q54, Q55, Q56, Q57, Q58, Q59, Q60, Q61, Q62, Q63, Q64, Q65, Q66, Q67, Q68, Q69, Q70, Q71, Q72]), "chamferType" : ChamferType.TWO_OFFSETS, "width1" : 1.27 * mm, "oppositeDirection" : false, "width2" : 2.54 * mm, "tangentPropagation" : true});
        }
        {
            var Q0;
            Q0=makeQuery(id+"F1.opExtrude","SWEPT_EDGE",EDGE,{"disambiguationData":[OSD([sQuery(id+"F0.wireOp",EDGE,"E59.MirrorCS"),sQuery(id+"F0.wireOp",EDGE,"E132.MirrorCS")])]});
            var Q1;
            Q1=makeQuery(id+"F1.opExtrude","SWEPT_EDGE",EDGE,{"disambiguationData":[OSD([sQuery(id+"F0.wireOp",EDGE,"E55.MirrorCS"),sQuery(id+"F0.wireOp",EDGE,"E126.MirrorCS")])]});
            var Q2;
            Q2=makeQuery(id+"F1.opExtrude","SWEPT_EDGE",EDGE,{"disambiguationData":[OSD([sQuery(id+"F0.wireOp",EDGE,"E63.MirrorCS"),sQuery(id+"F0.wireOp",EDGE,"E130.MirrorCS")])]});
            var Q3;
            Q3=makeQuery(id+"F1.opExtrude","SWEPT_EDGE",EDGE,{"disambiguationData":[OSD([sQuery(id+"F0.wireOp",EDGE,"E87.MirrorCS"),sQuery(id+"F0.wireOp",EDGE,"E108.MirrorCS")])]});
            var Q4;
            Q4=makeQuery(id+"F1.opExtrude","SWEPT_EDGE",EDGE,{"disambiguationData":[OSD([sQuery(id+"F0.wireOp",EDGE,"E12.MirrorCS"),sQuery(id+"F0.wireOp",EDGE,"E116.MirrorCS")])]});
            var Q5;
            Q5=makeQuery(id+"F1.opExtrude","SWEPT_EDGE",EDGE,{"disambiguationData":[OSD([sQuery(id+"F0.wireOp",EDGE,"E14.MirrorCS"),sQuery(id+"F0.wireOp",EDGE,"E118.MirrorCS")])]});
            var Q6;
            Q6=makeQuery(id+"F1.opExtrude","SWEPT_EDGE",EDGE,{"disambiguationData":[OSD([sQuery(id+"F0.wireOp",EDGE,"E85.MirrorCS"),sQuery(id+"F0.wireOp",EDGE,"E110.MirrorCS")])]});
            var Q7;
            Q7=makeQuery(id+"F1.opExtrude","SWEPT_EDGE",EDGE,{"disambiguationData":[OSD([sQuery(id+"F0.wireOp",EDGE,"E52.MirrorCS"),sQuery(id+"F0.wireOp",EDGE,"E123.MirrorCS")])]});
            var Q8;
            Q8=makeQuery(id+"F1.opExtrude","SWEPT_EDGE",EDGE,{"disambiguationData":[OSD([sQuery(id+"F0.wireOp",EDGE,"E60.MirrorCS"),sQuery(id+"F0.wireOp",EDGE,"E133.MirrorCS")])]});
            var Q9;
            Q9=makeQuery(id+"F1.opExtrude","SWEPT_EDGE",EDGE,{"disambiguationData":[OSD([sQuery(id+"F0.wireOp",EDGE,"E56.MirrorCS"),sQuery(id+"F0.wireOp",EDGE,"E127.MirrorCS")])]});
            var Q10;
            Q10=makeQuery(id+"F1.opExtrude","SWEPT_EDGE",EDGE,{"disambiguationData":[OSD([sQuery(id+"F0.wireOp",EDGE,"E64.MirrorCS"),sQuery(id+"F0.wireOp",EDGE,"E131.MirrorCS")])]});
            var Q11;
            Q11=makeQuery(id+"F1.opExtrude","SWEPT_EDGE",EDGE,{"disambiguationData":[OSD([sQuery(id+"F0.wireOp",EDGE,"E53.MirrorCS"),sQuery(id+"F0.wireOp",EDGE,"E124.MirrorCS")])]});
            var Q12;
            Q12=makeQuery(id+"F1.opExtrude","SWEPT_EDGE",EDGE,{"disambiguationData":[OSD([sQuery(id+"F0.wireOp",EDGE,"E17.MirrorCS"),sQuery(id+"F0.wireOp",EDGE,"E121.MirrorCS")])]});
            var Q13;
            Q13=makeQuery(id+"F1.opExtrude","SWEPT_EDGE",EDGE,{"disambiguationData":[OSD([sQuery(id+"F0.wireOp",EDGE,"E82.MirrorCS"),sQuery(id+"F0.wireOp",EDGE,"E113.MirrorCS")])]});
            var Q14;
            Q14=makeQuery(id+"F1.opExtrude","SWEPT_EDGE",EDGE,{"disambiguationData":[OSD([sQuery(id+"F0.wireOp",EDGE,"E54.MirrorCS"),sQuery(id+"F0.wireOp",EDGE,"E125.MirrorCS")])]});
            var Q15;
            Q15=makeQuery(id+"F1.opExtrude","SWEPT_EDGE",EDGE,{"disambiguationData":[OSD([sQuery(id+"F0.wireOp",EDGE,"E62.MirrorCS"),sQuery(id+"F0.wireOp",EDGE,"E137.MirrorCS")])]});
            var Q16;
            Q16=makeQuery(id+"F1.opExtrude","SWEPT_EDGE",EDGE,{"disambiguationData":[OSD([sQuery(id+"F0.wireOp",EDGE,"E84.MirrorCS"),sQuery(id+"F0.wireOp",EDGE,"E111.MirrorCS")])]});
            var Q17;
            Q17=makeQuery(id+"F1.opExtrude","SWEPT_EDGE",EDGE,{"disambiguationData":[OSD([sQuery(id+"F0.wireOp",EDGE,"E15.MirrorCS"),sQuery(id+"F0.wireOp",EDGE,"E119.MirrorCS")])]});
            var Q18;
            Q18=makeQuery(id+"F1.opExtrude","SWEPT_EDGE",EDGE,{"disambiguationData":[OSD([sQuery(id+"F0.wireOp",EDGE,"E57.MirrorCS"),sQuery(id+"F0.wireOp",EDGE,"E128.MirrorCS")])]});
            var Q19;
            Q19=makeQuery(id+"F1.opExtrude","SWEPT_EDGE",EDGE,{"disambiguationData":[OSD([sQuery(id+"F0.wireOp",EDGE,"E65.MirrorCS"),sQuery(id+"F0.wireOp",EDGE,"E134.MirrorCS")])]});
            var Q20;
            Q20=makeQuery(id+"F1.opExtrude","SWEPT_EDGE",EDGE,{"disambiguationData":[OSD([sQuery(id+"F0.wireOp",EDGE,"E9.0.1.0"),sQuery(id+"F0.wireOp",EDGE,"E9.0.1.1")])]});
            var Q21;
            Q21=makeQuery(id+"F1.opExtrude","SWEPT_EDGE",EDGE,{"disambiguationData":[OSD([sQuery(id+"F0.wireOp",EDGE,"E89.MirrorCS"),sQuery(id+"F0.wireOp",EDGE,"E106.MirrorCS")])]});
            var Q22;
            Q22=makeQuery(id+"F1.opExtrude","SWEPT_EDGE",EDGE,{"disambiguationData":[OSD([sQuery(id+"F0.wireOp",EDGE,"E18.MirrorCS"),sQuery(id+"F0.wireOp",EDGE,"E114.MirrorCS")])]});
            var Q23;
            Q23=makeQuery(id+"F1.opExtrude","SWEPT_EDGE",EDGE,{"disambiguationData":[OSD([sQuery(id+"F0.wireOp",EDGE,"E86.MirrorCS"),sQuery(id+"F0.wireOp",EDGE,"E109.MirrorCS")])]});
            var Q24;
            Q24=makeQuery(id+"F1.opExtrude","SWEPT_EDGE",EDGE,{"disambiguationData":[OSD([sQuery(id+"F0.wireOp",EDGE,"E13.MirrorCS"),sQuery(id+"F0.wireOp",EDGE,"E117.MirrorCS")])]});
            var Q25;
            Q25=makeQuery(id+"F1.opExtrude","SWEPT_EDGE",EDGE,{"disambiguationData":[OSD([sQuery(id+"F0.wireOp",EDGE,"E88.MirrorCS"),sQuery(id+"F0.wireOp",EDGE,"E107.MirrorCS")])]});
            var Q26;
            Q26=makeQuery(id+"F1.opExtrude","SWEPT_EDGE",EDGE,{"disambiguationData":[OSD([sQuery(id+"F0.wireOp",EDGE,"E11.MirrorCS"),sQuery(id+"F0.wireOp",EDGE,"E115.MirrorCS")])]});
            var Q27;
            Q27=makeQuery(id+"F1.opExtrude","SWEPT_EDGE",EDGE,{"disambiguationData":[OSD([sQuery(id+"F0.wireOp",EDGE,"E83.MirrorCS"),sQuery(id+"F0.wireOp",EDGE,"E112.MirrorCS")])]});
            var Q28;
            Q28=makeQuery(id+"F1.opExtrude","SWEPT_EDGE",EDGE,{"disambiguationData":[OSD([sQuery(id+"F0.wireOp",EDGE,"E16.MirrorCS"),sQuery(id+"F0.wireOp",EDGE,"E120.MirrorCS")])]});
            var Q29;
            Q29=makeQuery(id+"F1.opExtrude","SWEPT_EDGE",EDGE,{"disambiguationData":[OSD([sQuery(id+"F0.wireOp",EDGE,"E66.MirrorCS"),sQuery(id+"F0.wireOp",EDGE,"E135.MirrorCS")])]});
            var Q30;
            Q30=makeQuery(id+"F1.opExtrude","SWEPT_EDGE",EDGE,{"disambiguationData":[OSD([sQuery(id+"F0.wireOp",EDGE,"E58.MirrorCS"),sQuery(id+"F0.wireOp",EDGE,"E129.MirrorCS")])]});
            var Q31;
            Q31=makeQuery(id+"F1.opExtrude","SWEPT_EDGE",EDGE,{"disambiguationData":[OSD([sQuery(id+"F0.wireOp",EDGE,"E9.2.3.4"),sQuery(id+"F0.wireOp",EDGE,"E9.2.3.7")])]});
            var Q32;
            Q32=makeQuery(id+"F1.opExtrude","SWEPT_EDGE",EDGE,{"disambiguationData":[OSD([sQuery(id+"F0.wireOp",EDGE,"E9.2.3.0"),sQuery(id+"F0.wireOp",EDGE,"E9.2.3.1")])]});
            var Q33;
            Q33=makeQuery(id+"F1.opExtrude","SWEPT_EDGE",EDGE,{"disambiguationData":[OSD([sQuery(id+"F0.wireOp",EDGE,"E9.1.3.4"),sQuery(id+"F0.wireOp",EDGE,"E9.1.3.7")])]});
            var Q34;
            Q34=makeQuery(id+"F1.opExtrude","SWEPT_EDGE",EDGE,{"disambiguationData":[OSD([sQuery(id+"F0.wireOp",EDGE,"E9.1.3.0"),sQuery(id+"F0.wireOp",EDGE,"E9.1.3.1")])]});
            var Q35;
            Q35=makeQuery(id+"F1.opExtrude","SWEPT_EDGE",EDGE,{"disambiguationData":[OSD([sQuery(id+"F0.wireOp",EDGE,"E9.1.2.0"),sQuery(id+"F0.wireOp",EDGE,"E9.1.2.1")])]});
            var Q36;
            Q36=makeQuery(id+"F1.opExtrude","SWEPT_EDGE",EDGE,{"disambiguationData":[OSD([sQuery(id+"F0.wireOp",EDGE,"E9.1.2.4"),sQuery(id+"F0.wireOp",EDGE,"E9.1.2.7")])]});
            var Q37;
            Q37=makeQuery(id+"F1.opExtrude","SWEPT_EDGE",EDGE,{"disambiguationData":[OSD([sQuery(id+"F0.wireOp",EDGE,"E9.2.2.0"),sQuery(id+"F0.wireOp",EDGE,"E9.2.2.1")])]});
            var Q38;
            Q38=makeQuery(id+"F1.opExtrude","SWEPT_EDGE",EDGE,{"disambiguationData":[OSD([sQuery(id+"F0.wireOp",EDGE,"E9.2.2.4"),sQuery(id+"F0.wireOp",EDGE,"E9.2.2.7")])]});
            var Q39;
            Q39=makeQuery(id+"F1.opExtrude","SWEPT_EDGE",EDGE,{"disambiguationData":[OSD([sQuery(id+"F0.wireOp",EDGE,"E9.3.3.0"),sQuery(id+"F0.wireOp",EDGE,"E9.3.3.1")])]});
            var Q40;
            Q40=makeQuery(id+"F1.opExtrude","SWEPT_EDGE",EDGE,{"disambiguationData":[OSD([sQuery(id+"F0.wireOp",EDGE,"E9.3.2.0"),sQuery(id+"F0.wireOp",EDGE,"E9.3.2.1")])]});
            var Q41;
            Q41=makeQuery(id+"F1.opExtrude","SWEPT_EDGE",EDGE,{"disambiguationData":[OSD([sQuery(id+"F0.wireOp",EDGE,"E9.4.3.0"),sQuery(id+"F0.wireOp",EDGE,"E9.4.3.1")])]});
            var Q42;
            Q42=makeQuery(id+"F1.opExtrude","SWEPT_EDGE",EDGE,{"disambiguationData":[OSD([sQuery(id+"F0.wireOp",EDGE,"E9.4.3.4"),sQuery(id+"F0.wireOp",EDGE,"E9.4.3.7")])]});
            var Q43;
            Q43=makeQuery(id+"F1.opExtrude","SWEPT_EDGE",EDGE,{"disambiguationData":[OSD([sQuery(id+"F0.wireOp",EDGE,"E9.3.3.4"),sQuery(id+"F0.wireOp",EDGE,"E9.3.3.7")])]});
            var Q44;
            Q44=makeQuery(id+"F1.opExtrude","SWEPT_EDGE",EDGE,{"disambiguationData":[OSD([sQuery(id+"F0.wireOp",EDGE,"E9.4.2.0"),sQuery(id+"F0.wireOp",EDGE,"E9.4.2.1")])]});
            var Q45;
            Q45=makeQuery(id+"F1.opExtrude","SWEPT_EDGE",EDGE,{"disambiguationData":[OSD([sQuery(id+"F0.wireOp",EDGE,"E9.4.2.4"),sQuery(id+"F0.wireOp",EDGE,"E9.4.2.7")])]});
            var Q46;
            Q46=makeQuery(id+"F1.opExtrude","SWEPT_EDGE",EDGE,{"disambiguationData":[OSD([sQuery(id+"F0.wireOp",EDGE,"E9.3.2.4"),sQuery(id+"F0.wireOp",EDGE,"E9.3.2.7")])]});
            var Q47;
            Q47=makeQuery(id+"F1.opExtrude","SWEPT_EDGE",EDGE,{"disambiguationData":[OSD([sQuery(id+"F0.wireOp",EDGE,"E9.3.0.4"),sQuery(id+"F0.wireOp",EDGE,"E9.3.0.7")])]});
            var Q48;
            Q48=makeQuery(id+"F1.opExtrude","SWEPT_EDGE",EDGE,{"disambiguationData":[OSD([sQuery(id+"F0.wireOp",EDGE,"E9.3.0.0"),sQuery(id+"F0.wireOp",EDGE,"E9.3.0.1")])]});
            var Q49;
            Q49=makeQuery(id+"F1.opExtrude","SWEPT_EDGE",EDGE,{"disambiguationData":[OSD([sQuery(id+"F0.wireOp",EDGE,"E9.4.0.0"),sQuery(id+"F0.wireOp",EDGE,"E9.4.0.1")])]});
            var Q50;
            Q50=makeQuery(id+"F1.opExtrude","SWEPT_EDGE",EDGE,{"disambiguationData":[OSD([sQuery(id+"F0.wireOp",EDGE,"E9.4.0.4"),sQuery(id+"F0.wireOp",EDGE,"E9.4.0.7")])]});
            var Q51;
            Q51=makeQuery(id+"F1.opExtrude","SWEPT_EDGE",EDGE,{"disambiguationData":[OSD([sQuery(id+"F0.wireOp",EDGE,"E9.2.0.4"),sQuery(id+"F0.wireOp",EDGE,"E9.2.0.7")])]});
            var Q52;
            Q52=makeQuery(id+"F1.opExtrude","SWEPT_EDGE",EDGE,{"disambiguationData":[OSD([sQuery(id+"F0.wireOp",EDGE,"E9.2.0.0"),sQuery(id+"F0.wireOp",EDGE,"E9.2.0.1")])]});
            var Q53;
            Q53=makeQuery(id+"F1.opExtrude","SWEPT_EDGE",EDGE,{"disambiguationData":[OSD([sQuery(id+"F0.wireOp",EDGE,"E9.2.1.0"),sQuery(id+"F0.wireOp",EDGE,"E9.2.1.1")])]});
            var Q54;
            Q54=makeQuery(id+"F1.opExtrude","SWEPT_EDGE",EDGE,{"disambiguationData":[OSD([sQuery(id+"F0.wireOp",EDGE,"E9.1.1.4"),sQuery(id+"F0.wireOp",EDGE,"E9.1.1.7")])]});
            var Q55;
            Q55=makeQuery(id+"F1.opExtrude","SWEPT_EDGE",EDGE,{"disambiguationData":[OSD([sQuery(id+"F0.wireOp",EDGE,"E9.3.1.0"),sQuery(id+"F0.wireOp",EDGE,"E9.3.1.1")])]});
            var Q56;
            Q56=makeQuery(id+"F1.opExtrude","SWEPT_EDGE",EDGE,{"disambiguationData":[OSD([sQuery(id+"F0.wireOp",EDGE,"E9.3.1.4"),sQuery(id+"F0.wireOp",EDGE,"E9.3.1.7")])]});
            var Q57;
            Q57=makeQuery(id+"F1.opExtrude","SWEPT_EDGE",EDGE,{"disambiguationData":[OSD([sQuery(id+"F0.wireOp",EDGE,"E9.4.1.0"),sQuery(id+"F0.wireOp",EDGE,"E9.4.1.1")])]});
            var Q58;
            Q58=makeQuery(id+"F1.opExtrude","SWEPT_EDGE",EDGE,{"disambiguationData":[OSD([sQuery(id+"F0.wireOp",EDGE,"E9.4.1.4"),sQuery(id+"F0.wireOp",EDGE,"E9.4.1.7")])]});
            var Q59;
            Q59=makeQuery(id+"F1.opExtrude","SWEPT_EDGE",EDGE,{"disambiguationData":[OSD([sQuery(id+"F0.wireOp",EDGE,"E9.1.0.0"),sQuery(id+"F0.wireOp",EDGE,"E9.1.0.1")])]});
            var Q60;
            Q60=makeQuery(id+"F1.opExtrude","SWEPT_EDGE",EDGE,{"disambiguationData":[OSD([sQuery(id+"F0.wireOp",EDGE,"E9.1.0.4"),sQuery(id+"F0.wireOp",EDGE,"E9.1.0.7")])]});
            var Q61;
            Q61=makeQuery(id+"F1.opExtrude","SWEPT_EDGE",EDGE,{"disambiguationData":[OSD([sQuery(id+"F0.wireOp",EDGE,"E7.MirrorCS"),sQuery(id+"F0.wireOp",EDGE,"E8.MirrorCS")])]});
            var Q62;
            Q62=makeQuery(id+"F1.opExtrude","SWEPT_EDGE",EDGE,{"disambiguationData":[OSD([sQuery(id+"F0.wireOp",EDGE,"E2"),sQuery(id+"F0.wireOp",EDGE,"E3.left")])]});
            var Q63;
            Q63=makeQuery(id+"F1.opExtrude","SWEPT_EDGE",EDGE,{"disambiguationData":[OSD([sQuery(id+"F0.wireOp",EDGE,"E9.0.1.4"),sQuery(id+"F0.wireOp",EDGE,"E9.0.1.7")])]});
            var Q64;
            Q64=makeQuery(id+"F1.opExtrude","SWEPT_EDGE",EDGE,{"disambiguationData":[OSD([sQuery(id+"F0.wireOp",EDGE,"E9.1.1.0"),sQuery(id+"F0.wireOp",EDGE,"E9.1.1.1")])]});
            var Q65;
            Q65=makeQuery(id+"F1.opExtrude","SWEPT_EDGE",EDGE,{"disambiguationData":[OSD([sQuery(id+"F0.wireOp",EDGE,"E9.0.2.0"),sQuery(id+"F0.wireOp",EDGE,"E9.0.2.1")])]});
            var Q66;
            Q66=makeQuery(id+"F1.opExtrude","SWEPT_EDGE",EDGE,{"disambiguationData":[OSD([sQuery(id+"F0.wireOp",EDGE,"E9.0.2.4"),sQuery(id+"F0.wireOp",EDGE,"E9.0.2.7")])]});
            var Q67;
            Q67=makeQuery(id+"F1.opExtrude","SWEPT_EDGE",EDGE,{"disambiguationData":[OSD([sQuery(id+"F0.wireOp",EDGE,"E9.0.3.0"),sQuery(id+"F0.wireOp",EDGE,"E9.0.3.1")])]});
            var Q68;
            Q68=makeQuery(id+"F1.opExtrude","SWEPT_EDGE",EDGE,{"disambiguationData":[OSD([sQuery(id+"F0.wireOp",EDGE,"E9.0.3.4"),sQuery(id+"F0.wireOp",EDGE,"E9.0.3.7")])]});
            var Q69;
            Q69=makeQuery(id+"F1.opExtrude","SWEPT_EDGE",EDGE,{"disambiguationData":[OSD([sQuery(id+"F0.wireOp",EDGE,"E9.2.1.4"),sQuery(id+"F0.wireOp",EDGE,"E9.2.1.7")])]});
            var Q70;
            Q70=makeQuery(id+"F1.opExtrude","SWEPT_EDGE",EDGE,{"disambiguationData":[OSD([sQuery(id+"F0.wireOp",EDGE,"E61.MirrorCS"),sQuery(id+"F0.wireOp",EDGE,"E136.MirrorCS")])]});
            chamfer(context, id + "F17", {"entities" : qUnion([Q0, Q1, Q2, Q3, Q4, Q5, Q6, Q7, Q8, Q9, Q10, Q11, Q12, Q13, Q14, Q15, Q16, Q17, Q18, Q19, Q20, Q21, Q22, Q23, Q24, Q25, Q26, Q27, Q28, Q29, Q30, Q31, Q32, Q33, Q34, Q35, Q36, Q37, Q38, Q39, Q40, Q41, Q42, Q43, Q44, Q45, Q46, Q47, Q48, Q49, Q50, Q51, Q52, Q53, Q54, Q55, Q56, Q57, Q58, Q59, Q60, Q61, Q62, Q63, Q64, Q65, Q66, Q67, Q68, Q69, Q70]), "chamferType" : ChamferType.TWO_OFFSETS, "width1" : 2.54 * mm, "oppositeDirection" : false, "width2" : 1.27 * mm, "tangentPropagation" : true});
        }
        {
            var Q0;
            Q0=makeQuery(id+"F3.opExtrude","SWEPT_FACE",FACE,{"disambiguationData":[OSD([sQuery(id+"F2.wireOp",EDGE,"E139.bottom")])]});
            var sketch = newSketch(context, id + "F18", { "sketchPlane" : qUnion([Q0])});
            skLineSegment(sketch, "E217.0", {"start": v(130.21, -22.23) * mm, "end": v(111.09, -22.23) * mm});
            skLineSegment(sketch, "E218.0", {"start": v(111.09, -22.23) * mm, "end": v(111.09, -25.4) * mm});
            skLineSegment(sketch, "E219.0", {"start": v(130.21, -22.23) * mm, "end": v(130.21, -25.4) * mm});
            skLineSegment(sketch, "E220", {"start": v(130.21, -25.4) * mm, "end": v(111.09, -25.4) * mm});
            skLineSegment(sketch, "E221.0", {"start": v(-111.09, -22.23) * mm, "end": v(-130.21, -22.23) * mm});
            skLineSegment(sketch, "E222.0", {"start": v(-130.21, -22.23) * mm, "end": v(-130.21, -25.4) * mm});
            skLineSegment(sketch, "E223.0", {"start": v(-111.09, -22.23) * mm, "end": v(-111.09, -25.4) * mm});
            skLineSegment(sketch, "E224", {"start": v(-111.09, -25.4) * mm, "end": v(-130.21, -25.4) * mm});
            skSolve(sketch);
        }
        {
            var Q0;
            Q0 = qSketchRegion(id + "F18", true);
            var Q1;
            Q1=makeQuery(id+"F3.opExtrude","SWEPT_FACE",FACE,{"disambiguationData":[OSD([sQuery(id+"F2.wireOp",EDGE,"E139.top")])]});
            extrude(context, id + "F19", {"entities" : qUnion([Q0]), "operationType" : NewBodyOperationType.ADD, "endBound" : BoundingType.UP_TO_SURFACE, "oppositeDirection" : true, "endBoundEntityFace" : qUnion([Q1]), "depth" : 25.4 * mm});
        }
    });
